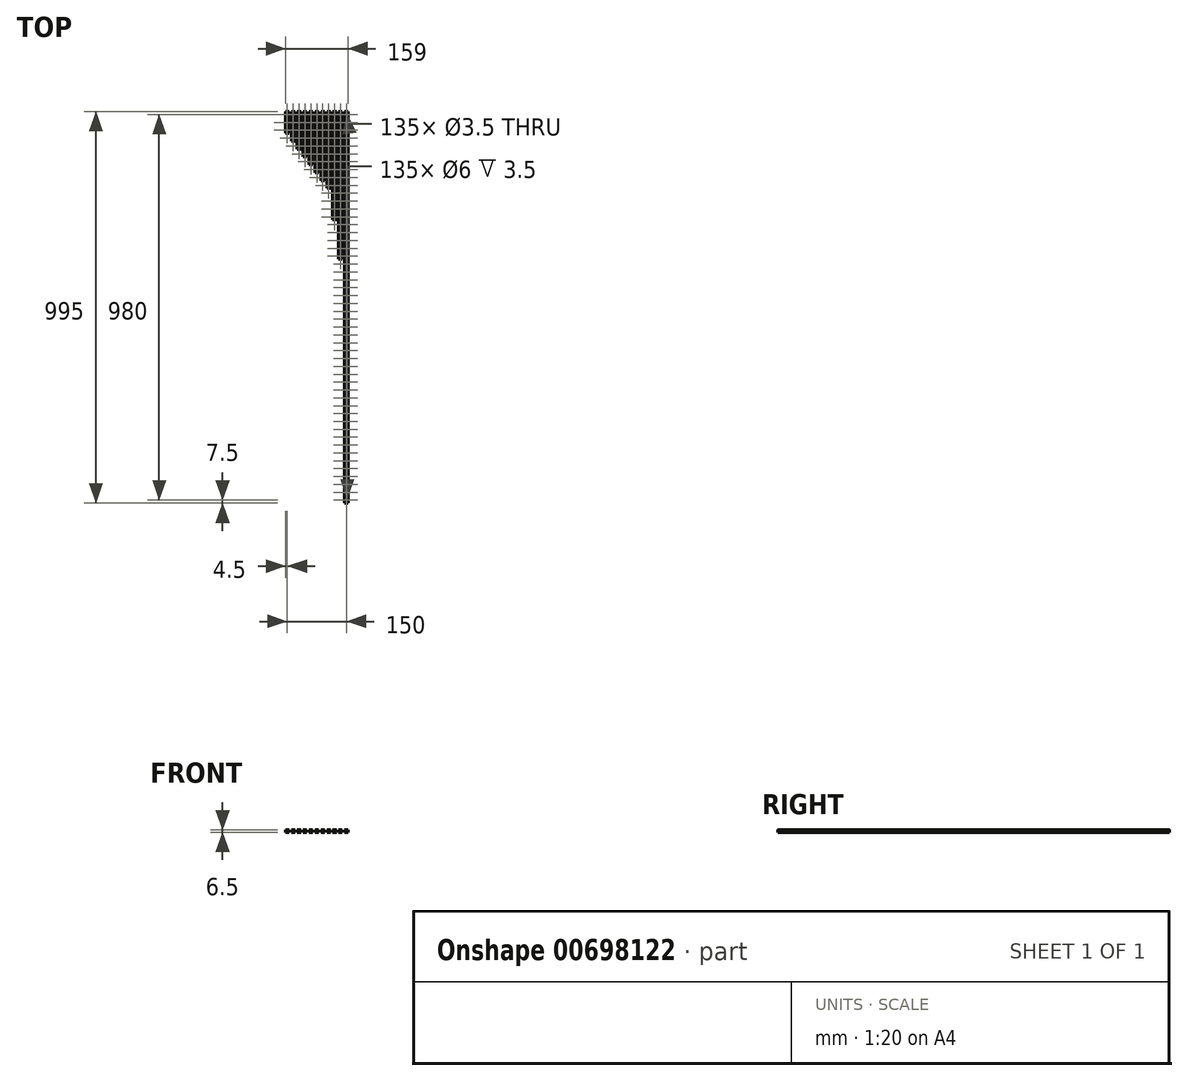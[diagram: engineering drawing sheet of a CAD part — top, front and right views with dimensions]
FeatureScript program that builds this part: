
annotation { "Feature Type Name" : "Feature", "Feature Type Description" : "" }
export const myFeature = defineFeature(function(context is Context, id is Id, definition is map)
    precondition{}
    {
        {
            var Q0;
            Q0=qCreatedBy(makeId("Front.planeOp"),FACE);
            var sketch = newSketch(context, id + "F0", { "sketchPlane" : qUnion([Q0])});
            skPoint(sketch, "E0.middle", {"position": v(0, 0) * mm});
            skLineSegment(sketch, "E1.bottom", {"start": v(4.15, -3.25) * mm, "end": v(-4.15, -3.25) * mm});
            skLineSegment(sketch, "E1.top", {"start": v(4.15, 3.25) * mm, "end": v(-4.15, 3.25) * mm});
            skLineSegment(sketch, "E1.left", {"start": v(4.5, -2.9) * mm, "end": v(4.5, 0.28) * mm});
            skLineSegment(sketch, "E1.right", {"start": v(-4.5, -2.9) * mm, "end": v(-4.5, 0.28) * mm});
            skArc(sketch, "E2", {"start": v(-4.5, 0.28) * mm, "mid": v(-4.1, 0.49) * mm, "end": v(-3.83, 0.85) * mm});
            skArc(sketch, "E3", {"start": v(4.5, 2.22) * mm, "mid": v(4.1, 2.01) * mm, "end": v(3.83, 1.65) * mm});
            skLineSegment(sketch, "E4", {"start": v(3.3, 1.65) * mm, "end": v(3.83, 1.65) * mm});
            skLineSegment(sketch, "E5", {"start": v(3.3, 0.85) * mm, "end": v(3.83, 0.85) * mm});
            skLineSegment(sketch, "E6", {"start": v(-3.3, 0.85) * mm, "end": v(-3.83, 0.85) * mm});
            skLineSegment(sketch, "E7", {"start": v(-3.3, 1.65) * mm, "end": v(-3.83, 1.65) * mm});
            skLineSegment(sketch, "E8", {"start": v(-4.5, 2.9) * mm, "end": v(-4.15, 3.25) * mm});
            skLineSegment(sketch, "E9.MirrorCS", {"start": v(4.5, 2.9) * mm, "end": v(4.15, 3.25) * mm});
            skLineSegment(sketch, "E10.MirrorCS", {"start": v(4.5, -2.9) * mm, "end": v(4.15, -3.25) * mm});
            skLineSegment(sketch, "E11.MirrorCS", {"start": v(-4.5, -2.9) * mm, "end": v(-4.15, -3.25) * mm});
            skPoint(sketch, "E12.orphan", {"position": v(-4.5, 3.25) * mm});
            skLineSegment(sketch, "E13.trimOffspring", {"start": v(-4.5, 2.22) * mm, "end": v(-4.5, 2.9) * mm});
            skArc(sketch, "E14.trimOffspring", {"start": v(-3.83, 1.65) * mm, "mid": v(-4.1, 2.01) * mm, "end": v(-4.5, 2.22) * mm});
            skPoint(sketch, "E15.orphan", {"position": v(4.5, 3.25) * mm});
            skLineSegment(sketch, "E16.trimOffspring", {"start": v(4.5, 2.22) * mm, "end": v(4.5, 2.9) * mm});
            skArc(sketch, "E17.trimOffspring", {"start": v(3.83, 0.85) * mm, "mid": v(4.1, 0.49) * mm, "end": v(4.5, 0.28) * mm});
            skPoint(sketch, "E18.orphan", {"position": v(4.5, -3.25) * mm});
            skPoint(sketch, "E19.orphan", {"position": v(-4.5, -3.25) * mm});
            skLineSegment(sketch, "E20", {"start": v(-3.3, 1.65) * mm, "end": v(-3.3, 0.85) * mm});
            skLineSegment(sketch, "E21", {"start": v(3.3, 1.65) * mm, "end": v(3.3, 0.85) * mm});
            skLineSegment(sketch, "E22", {"start": v(-4.75, 1.25) * mm, "end": v(4.75, 1.25) * mm, "construction": true});
            skLineSegment(sketch, "E23.1.0.0", {"start": v(10.25, 1.25) * mm, "end": v(19.75, 1.25) * mm, "construction": true});
            skLineSegment(sketch, "E23.1.0.1", {"start": v(10.5, -2.9) * mm, "end": v(10.5, 0.28) * mm});
            skLineSegment(sketch, "E23.1.0.2", {"start": v(19.5, -2.9) * mm, "end": v(19.5, 0.28) * mm});
            skLineSegment(sketch, "E23.1.0.3", {"start": v(19.15, -3.25) * mm, "end": v(10.85, -3.25) * mm});
            skLineSegment(sketch, "E23.1.0.4", {"start": v(19.15, 3.25) * mm, "end": v(10.85, 3.25) * mm});
            skPoint(sketch, "E23.1.0.5", {"position": v(15, 0) * mm});
            skPoint(sketch, "E23.1.0.6", {"position": v(10.5, -3.25) * mm});
            skPoint(sketch, "E23.1.0.7", {"position": v(10.5, 3.25) * mm});
            skPoint(sketch, "E23.1.0.8", {"position": v(19.5, 3.25) * mm});
            skPoint(sketch, "E23.1.0.9", {"position": v(19.5, -3.25) * mm});
            skPoint(sketch, "E23.1.0.10", {"position": v(15, 0) * mm});
            skLineSegment(sketch, "E23.1.0.11", {"start": v(19.5, -2.9) * mm, "end": v(19.15, -3.25) * mm});
            skLineSegment(sketch, "E23.1.0.12", {"start": v(19.5, 2.9) * mm, "end": v(19.15, 3.25) * mm});
            skLineSegment(sketch, "E23.1.0.13", {"start": v(10.5, -2.9) * mm, "end": v(10.85, -3.25) * mm});
            skLineSegment(sketch, "E23.1.0.14", {"start": v(11.7, 1.65) * mm, "end": v(11.17, 1.65) * mm});
            skLineSegment(sketch, "E23.1.0.15", {"start": v(10.5, 2.22) * mm, "end": v(10.5, 2.9) * mm});
            skLineSegment(sketch, "E23.1.0.16", {"start": v(19.5, 2.22) * mm, "end": v(19.5, 2.9) * mm});
            skArc(sketch, "E23.1.0.17", {"start": v(18.83, 0.85) * mm, "mid": v(19.1, 0.49) * mm, "end": v(19.5, 0.28) * mm});
            skLineSegment(sketch, "E23.1.0.18", {"start": v(11.7, 1.65) * mm, "end": v(11.7, 0.85) * mm});
            skLineSegment(sketch, "E23.1.0.19", {"start": v(18.3, 0.85) * mm, "end": v(18.83, 0.85) * mm});
            skLineSegment(sketch, "E23.1.0.20", {"start": v(11.7, 0.85) * mm, "end": v(11.17, 0.85) * mm});
            skArc(sketch, "E23.1.0.21", {"start": v(10.5, 0.28) * mm, "mid": v(10.9, 0.49) * mm, "end": v(11.17, 0.85) * mm});
            skLineSegment(sketch, "E23.1.0.22", {"start": v(10.5, 2.9) * mm, "end": v(10.85, 3.25) * mm});
            skArc(sketch, "E23.1.0.23", {"start": v(11.17, 1.65) * mm, "mid": v(10.9, 2.01) * mm, "end": v(10.5, 2.22) * mm});
            skLineSegment(sketch, "E23.1.0.24", {"start": v(18.3, 1.65) * mm, "end": v(18.83, 1.65) * mm});
            skArc(sketch, "E23.1.0.25", {"start": v(19.5, 2.22) * mm, "mid": v(19.1, 2.01) * mm, "end": v(18.83, 1.65) * mm});
            skArc(sketch, "E23.1.0.26", {"start": v(18.83, 0.85) * mm, "mid": v(19.1, 0.49) * mm, "end": v(19.5, 0.28) * mm});
            skLineSegment(sketch, "E23.1.0.27", {"start": v(18.3, 1.65) * mm, "end": v(18.3, 0.85) * mm});
            skLineSegment(sketch, "E23.2.0.0", {"start": v(25.25, 1.25) * mm, "end": v(34.75, 1.25) * mm, "construction": true});
            skLineSegment(sketch, "E23.2.0.1", {"start": v(25.5, -2.9) * mm, "end": v(25.5, 0.28) * mm});
            skLineSegment(sketch, "E23.2.0.2", {"start": v(34.5, -2.9) * mm, "end": v(34.5, 0.28) * mm});
            skLineSegment(sketch, "E23.2.0.3", {"start": v(34.15, -3.25) * mm, "end": v(25.85, -3.25) * mm});
            skLineSegment(sketch, "E23.2.0.4", {"start": v(34.15, 3.25) * mm, "end": v(25.85, 3.25) * mm});
            skPoint(sketch, "E23.2.0.5", {"position": v(30, 0) * mm});
            skPoint(sketch, "E23.2.0.6", {"position": v(25.5, -3.25) * mm});
            skPoint(sketch, "E23.2.0.7", {"position": v(25.5, 3.25) * mm});
            skPoint(sketch, "E23.2.0.8", {"position": v(34.5, 3.25) * mm});
            skPoint(sketch, "E23.2.0.9", {"position": v(34.5, -3.25) * mm});
            skPoint(sketch, "E23.2.0.10", {"position": v(30, 0) * mm});
            skLineSegment(sketch, "E23.2.0.11", {"start": v(34.5, -2.9) * mm, "end": v(34.15, -3.25) * mm});
            skLineSegment(sketch, "E23.2.0.12", {"start": v(34.5, 2.9) * mm, "end": v(34.15, 3.25) * mm});
            skLineSegment(sketch, "E23.2.0.13", {"start": v(25.5, -2.9) * mm, "end": v(25.85, -3.25) * mm});
            skLineSegment(sketch, "E23.2.0.14", {"start": v(26.7, 1.65) * mm, "end": v(26.17, 1.65) * mm});
            skLineSegment(sketch, "E23.2.0.15", {"start": v(25.5, 2.22) * mm, "end": v(25.5, 2.9) * mm});
            skLineSegment(sketch, "E23.2.0.16", {"start": v(34.5, 2.22) * mm, "end": v(34.5, 2.9) * mm});
            skArc(sketch, "E23.2.0.17", {"start": v(33.83, 0.85) * mm, "mid": v(34.1, 0.49) * mm, "end": v(34.5, 0.28) * mm});
            skLineSegment(sketch, "E23.2.0.18", {"start": v(26.7, 1.65) * mm, "end": v(26.7, 0.85) * mm});
            skLineSegment(sketch, "E23.2.0.19", {"start": v(33.3, 0.85) * mm, "end": v(33.83, 0.85) * mm});
            skLineSegment(sketch, "E23.2.0.20", {"start": v(26.7, 0.85) * mm, "end": v(26.17, 0.85) * mm});
            skArc(sketch, "E23.2.0.21", {"start": v(25.5, 0.28) * mm, "mid": v(25.9, 0.49) * mm, "end": v(26.17, 0.85) * mm});
            skLineSegment(sketch, "E23.2.0.22", {"start": v(25.5, 2.9) * mm, "end": v(25.85, 3.25) * mm});
            skArc(sketch, "E23.2.0.23", {"start": v(26.17, 1.65) * mm, "mid": v(25.9, 2.01) * mm, "end": v(25.5, 2.22) * mm});
            skLineSegment(sketch, "E23.2.0.24", {"start": v(33.3, 1.65) * mm, "end": v(33.83, 1.65) * mm});
            skArc(sketch, "E23.2.0.25", {"start": v(34.5, 2.22) * mm, "mid": v(34.1, 2.01) * mm, "end": v(33.83, 1.65) * mm});
            skArc(sketch, "E23.2.0.26", {"start": v(33.83, 0.85) * mm, "mid": v(34.1, 0.49) * mm, "end": v(34.5, 0.28) * mm});
            skLineSegment(sketch, "E23.2.0.27", {"start": v(33.3, 1.65) * mm, "end": v(33.3, 0.85) * mm});
            skLineSegment(sketch, "E23.3.0.0", {"start": v(40.25, 1.25) * mm, "end": v(49.75, 1.25) * mm, "construction": true});
            skLineSegment(sketch, "E23.3.0.1", {"start": v(40.5, -2.9) * mm, "end": v(40.5, 0.28) * mm});
            skLineSegment(sketch, "E23.3.0.2", {"start": v(49.5, -2.9) * mm, "end": v(49.5, 0.28) * mm});
            skLineSegment(sketch, "E23.3.0.3", {"start": v(49.15, -3.25) * mm, "end": v(40.85, -3.25) * mm});
            skLineSegment(sketch, "E23.3.0.4", {"start": v(49.15, 3.25) * mm, "end": v(40.85, 3.25) * mm});
            skPoint(sketch, "E23.3.0.5", {"position": v(45, 0) * mm});
            skPoint(sketch, "E23.3.0.6", {"position": v(40.5, -3.25) * mm});
            skPoint(sketch, "E23.3.0.7", {"position": v(40.5, 3.25) * mm});
            skPoint(sketch, "E23.3.0.8", {"position": v(49.5, 3.25) * mm});
            skPoint(sketch, "E23.3.0.9", {"position": v(49.5, -3.25) * mm});
            skPoint(sketch, "E23.3.0.10", {"position": v(45, 0) * mm});
            skLineSegment(sketch, "E23.3.0.11", {"start": v(49.5, -2.9) * mm, "end": v(49.15, -3.25) * mm});
            skLineSegment(sketch, "E23.3.0.12", {"start": v(49.5, 2.9) * mm, "end": v(49.15, 3.25) * mm});
            skLineSegment(sketch, "E23.3.0.13", {"start": v(40.5, -2.9) * mm, "end": v(40.85, -3.25) * mm});
            skLineSegment(sketch, "E23.3.0.14", {"start": v(41.7, 1.65) * mm, "end": v(41.17, 1.65) * mm});
            skLineSegment(sketch, "E23.3.0.15", {"start": v(40.5, 2.22) * mm, "end": v(40.5, 2.9) * mm});
            skLineSegment(sketch, "E23.3.0.16", {"start": v(49.5, 2.22) * mm, "end": v(49.5, 2.9) * mm});
            skArc(sketch, "E23.3.0.17", {"start": v(48.83, 0.85) * mm, "mid": v(49.1, 0.49) * mm, "end": v(49.5, 0.28) * mm});
            skLineSegment(sketch, "E23.3.0.18", {"start": v(41.7, 1.65) * mm, "end": v(41.7, 0.85) * mm});
            skLineSegment(sketch, "E23.3.0.19", {"start": v(48.3, 0.85) * mm, "end": v(48.83, 0.85) * mm});
            skLineSegment(sketch, "E23.3.0.20", {"start": v(41.7, 0.85) * mm, "end": v(41.17, 0.85) * mm});
            skArc(sketch, "E23.3.0.21", {"start": v(40.5, 0.28) * mm, "mid": v(40.9, 0.49) * mm, "end": v(41.17, 0.85) * mm});
            skLineSegment(sketch, "E23.3.0.22", {"start": v(40.5, 2.9) * mm, "end": v(40.85, 3.25) * mm});
            skArc(sketch, "E23.3.0.23", {"start": v(41.17, 1.65) * mm, "mid": v(40.9, 2.01) * mm, "end": v(40.5, 2.22) * mm});
            skLineSegment(sketch, "E23.3.0.24", {"start": v(48.3, 1.65) * mm, "end": v(48.83, 1.65) * mm});
            skArc(sketch, "E23.3.0.25", {"start": v(49.5, 2.22) * mm, "mid": v(49.1, 2.01) * mm, "end": v(48.83, 1.65) * mm});
            skArc(sketch, "E23.3.0.26", {"start": v(48.83, 0.85) * mm, "mid": v(49.1, 0.49) * mm, "end": v(49.5, 0.28) * mm});
            skLineSegment(sketch, "E23.3.0.27", {"start": v(48.3, 1.65) * mm, "end": v(48.3, 0.85) * mm});
            skLineSegment(sketch, "E23.4.0.0", {"start": v(55.25, 1.25) * mm, "end": v(64.75, 1.25) * mm, "construction": true});
            skLineSegment(sketch, "E23.4.0.1", {"start": v(55.5, -2.9) * mm, "end": v(55.5, 0.28) * mm});
            skLineSegment(sketch, "E23.4.0.2", {"start": v(64.5, -2.9) * mm, "end": v(64.5, 0.28) * mm});
            skLineSegment(sketch, "E23.4.0.3", {"start": v(64.15, -3.25) * mm, "end": v(55.85, -3.25) * mm});
            skLineSegment(sketch, "E23.4.0.4", {"start": v(64.15, 3.25) * mm, "end": v(55.85, 3.25) * mm});
            skPoint(sketch, "E23.4.0.5", {"position": v(60, 0) * mm});
            skPoint(sketch, "E23.4.0.6", {"position": v(55.5, -3.25) * mm});
            skPoint(sketch, "E23.4.0.7", {"position": v(55.5, 3.25) * mm});
            skPoint(sketch, "E23.4.0.8", {"position": v(64.5, 3.25) * mm});
            skPoint(sketch, "E23.4.0.9", {"position": v(64.5, -3.25) * mm});
            skPoint(sketch, "E23.4.0.10", {"position": v(60, 0) * mm});
            skLineSegment(sketch, "E23.4.0.11", {"start": v(64.5, -2.9) * mm, "end": v(64.15, -3.25) * mm});
            skLineSegment(sketch, "E23.4.0.12", {"start": v(64.5, 2.9) * mm, "end": v(64.15, 3.25) * mm});
            skLineSegment(sketch, "E23.4.0.13", {"start": v(55.5, -2.9) * mm, "end": v(55.85, -3.25) * mm});
            skLineSegment(sketch, "E23.4.0.14", {"start": v(56.7, 1.65) * mm, "end": v(56.17, 1.65) * mm});
            skLineSegment(sketch, "E23.4.0.15", {"start": v(55.5, 2.22) * mm, "end": v(55.5, 2.9) * mm});
            skLineSegment(sketch, "E23.4.0.16", {"start": v(64.5, 2.22) * mm, "end": v(64.5, 2.9) * mm});
            skArc(sketch, "E23.4.0.17", {"start": v(63.83, 0.85) * mm, "mid": v(64.1, 0.49) * mm, "end": v(64.5, 0.28) * mm});
            skLineSegment(sketch, "E23.4.0.18", {"start": v(56.7, 1.65) * mm, "end": v(56.7, 0.85) * mm});
            skLineSegment(sketch, "E23.4.0.19", {"start": v(63.3, 0.85) * mm, "end": v(63.83, 0.85) * mm});
            skLineSegment(sketch, "E23.4.0.20", {"start": v(56.7, 0.85) * mm, "end": v(56.17, 0.85) * mm});
            skArc(sketch, "E23.4.0.21", {"start": v(55.5, 0.28) * mm, "mid": v(55.9, 0.49) * mm, "end": v(56.17, 0.85) * mm});
            skLineSegment(sketch, "E23.4.0.22", {"start": v(55.5, 2.9) * mm, "end": v(55.85, 3.25) * mm});
            skArc(sketch, "E23.4.0.23", {"start": v(56.17, 1.65) * mm, "mid": v(55.9, 2.01) * mm, "end": v(55.5, 2.22) * mm});
            skLineSegment(sketch, "E23.4.0.24", {"start": v(63.3, 1.65) * mm, "end": v(63.83, 1.65) * mm});
            skArc(sketch, "E23.4.0.25", {"start": v(64.5, 2.22) * mm, "mid": v(64.1, 2.01) * mm, "end": v(63.83, 1.65) * mm});
            skArc(sketch, "E23.4.0.26", {"start": v(63.83, 0.85) * mm, "mid": v(64.1, 0.49) * mm, "end": v(64.5, 0.28) * mm});
            skLineSegment(sketch, "E23.4.0.27", {"start": v(63.3, 1.65) * mm, "end": v(63.3, 0.85) * mm});
            skLineSegment(sketch, "E23.5.0.0", {"start": v(70.25, 1.25) * mm, "end": v(79.75, 1.25) * mm, "construction": true});
            skLineSegment(sketch, "E23.5.0.1", {"start": v(70.5, -2.9) * mm, "end": v(70.5, 0.28) * mm});
            skLineSegment(sketch, "E23.5.0.2", {"start": v(79.5, -2.9) * mm, "end": v(79.5, 0.28) * mm});
            skLineSegment(sketch, "E23.5.0.3", {"start": v(79.15, -3.25) * mm, "end": v(70.85, -3.25) * mm});
            skLineSegment(sketch, "E23.5.0.4", {"start": v(79.15, 3.25) * mm, "end": v(70.85, 3.25) * mm});
            skPoint(sketch, "E23.5.0.5", {"position": v(75, 0) * mm});
            skPoint(sketch, "E23.5.0.6", {"position": v(70.5, -3.25) * mm});
            skPoint(sketch, "E23.5.0.7", {"position": v(70.5, 3.25) * mm});
            skPoint(sketch, "E23.5.0.8", {"position": v(79.5, 3.25) * mm});
            skPoint(sketch, "E23.5.0.9", {"position": v(79.5, -3.25) * mm});
            skPoint(sketch, "E23.5.0.10", {"position": v(75, 0) * mm});
            skLineSegment(sketch, "E23.5.0.11", {"start": v(79.5, -2.9) * mm, "end": v(79.15, -3.25) * mm});
            skLineSegment(sketch, "E23.5.0.12", {"start": v(79.5, 2.9) * mm, "end": v(79.15, 3.25) * mm});
            skLineSegment(sketch, "E23.5.0.13", {"start": v(70.5, -2.9) * mm, "end": v(70.85, -3.25) * mm});
            skLineSegment(sketch, "E23.5.0.14", {"start": v(71.7, 1.65) * mm, "end": v(71.17, 1.65) * mm});
            skLineSegment(sketch, "E23.5.0.15", {"start": v(70.5, 2.22) * mm, "end": v(70.5, 2.9) * mm});
            skLineSegment(sketch, "E23.5.0.16", {"start": v(79.5, 2.22) * mm, "end": v(79.5, 2.9) * mm});
            skArc(sketch, "E23.5.0.17", {"start": v(78.83, 0.85) * mm, "mid": v(79.1, 0.49) * mm, "end": v(79.5, 0.28) * mm});
            skLineSegment(sketch, "E23.5.0.18", {"start": v(71.7, 1.65) * mm, "end": v(71.7, 0.85) * mm});
            skLineSegment(sketch, "E23.5.0.19", {"start": v(78.3, 0.85) * mm, "end": v(78.83, 0.85) * mm});
            skLineSegment(sketch, "E23.5.0.20", {"start": v(71.7, 0.85) * mm, "end": v(71.17, 0.85) * mm});
            skArc(sketch, "E23.5.0.21", {"start": v(70.5, 0.28) * mm, "mid": v(70.9, 0.49) * mm, "end": v(71.17, 0.85) * mm});
            skLineSegment(sketch, "E23.5.0.22", {"start": v(70.5, 2.9) * mm, "end": v(70.85, 3.25) * mm});
            skArc(sketch, "E23.5.0.23", {"start": v(71.17, 1.65) * mm, "mid": v(70.9, 2.01) * mm, "end": v(70.5, 2.22) * mm});
            skLineSegment(sketch, "E23.5.0.24", {"start": v(78.3, 1.65) * mm, "end": v(78.83, 1.65) * mm});
            skArc(sketch, "E23.5.0.25", {"start": v(79.5, 2.22) * mm, "mid": v(79.1, 2.01) * mm, "end": v(78.83, 1.65) * mm});
            skArc(sketch, "E23.5.0.26", {"start": v(78.83, 0.85) * mm, "mid": v(79.1, 0.49) * mm, "end": v(79.5, 0.28) * mm});
            skLineSegment(sketch, "E23.5.0.27", {"start": v(78.3, 1.65) * mm, "end": v(78.3, 0.85) * mm});
            skLineSegment(sketch, "E23.6.0.0", {"start": v(85.25, 1.25) * mm, "end": v(94.75, 1.25) * mm, "construction": true});
            skLineSegment(sketch, "E23.6.0.1", {"start": v(85.5, -2.9) * mm, "end": v(85.5, 0.28) * mm});
            skLineSegment(sketch, "E23.6.0.2", {"start": v(94.5, -2.9) * mm, "end": v(94.5, 0.28) * mm});
            skLineSegment(sketch, "E23.6.0.3", {"start": v(94.15, -3.25) * mm, "end": v(85.85, -3.25) * mm});
            skLineSegment(sketch, "E23.6.0.4", {"start": v(94.15, 3.25) * mm, "end": v(85.85, 3.25) * mm});
            skPoint(sketch, "E23.6.0.5", {"position": v(90, 0) * mm});
            skPoint(sketch, "E23.6.0.6", {"position": v(85.5, -3.25) * mm});
            skPoint(sketch, "E23.6.0.7", {"position": v(85.5, 3.25) * mm});
            skPoint(sketch, "E23.6.0.8", {"position": v(94.5, 3.25) * mm});
            skPoint(sketch, "E23.6.0.9", {"position": v(94.5, -3.25) * mm});
            skPoint(sketch, "E23.6.0.10", {"position": v(90, 0) * mm});
            skLineSegment(sketch, "E23.6.0.11", {"start": v(94.5, -2.9) * mm, "end": v(94.15, -3.25) * mm});
            skLineSegment(sketch, "E23.6.0.12", {"start": v(94.5, 2.9) * mm, "end": v(94.15, 3.25) * mm});
            skLineSegment(sketch, "E23.6.0.13", {"start": v(85.5, -2.9) * mm, "end": v(85.85, -3.25) * mm});
            skLineSegment(sketch, "E23.6.0.14", {"start": v(86.7, 1.65) * mm, "end": v(86.17, 1.65) * mm});
            skLineSegment(sketch, "E23.6.0.15", {"start": v(85.5, 2.22) * mm, "end": v(85.5, 2.9) * mm});
            skLineSegment(sketch, "E23.6.0.16", {"start": v(94.5, 2.22) * mm, "end": v(94.5, 2.9) * mm});
            skArc(sketch, "E23.6.0.17", {"start": v(93.83, 0.85) * mm, "mid": v(94.1, 0.49) * mm, "end": v(94.5, 0.28) * mm});
            skLineSegment(sketch, "E23.6.0.18", {"start": v(86.7, 1.65) * mm, "end": v(86.7, 0.85) * mm});
            skLineSegment(sketch, "E23.6.0.19", {"start": v(93.3, 0.85) * mm, "end": v(93.83, 0.85) * mm});
            skLineSegment(sketch, "E23.6.0.20", {"start": v(86.7, 0.85) * mm, "end": v(86.17, 0.85) * mm});
            skArc(sketch, "E23.6.0.21", {"start": v(85.5, 0.28) * mm, "mid": v(85.9, 0.49) * mm, "end": v(86.17, 0.85) * mm});
            skLineSegment(sketch, "E23.6.0.22", {"start": v(85.5, 2.9) * mm, "end": v(85.85, 3.25) * mm});
            skArc(sketch, "E23.6.0.23", {"start": v(86.17, 1.65) * mm, "mid": v(85.9, 2.01) * mm, "end": v(85.5, 2.22) * mm});
            skLineSegment(sketch, "E23.6.0.24", {"start": v(93.3, 1.65) * mm, "end": v(93.83, 1.65) * mm});
            skArc(sketch, "E23.6.0.25", {"start": v(94.5, 2.22) * mm, "mid": v(94.1, 2.01) * mm, "end": v(93.83, 1.65) * mm});
            skArc(sketch, "E23.6.0.26", {"start": v(93.83, 0.85) * mm, "mid": v(94.1, 0.49) * mm, "end": v(94.5, 0.28) * mm});
            skLineSegment(sketch, "E23.6.0.27", {"start": v(93.3, 1.65) * mm, "end": v(93.3, 0.85) * mm});
            skLineSegment(sketch, "E23.direction1", {"start": v(-4.5, -3.25) * mm, "end": v(10.5, -3.25) * mm, "construction": true});
            skLineSegment(sketch, "E24.0.7.0", {"start": v(100.25, 1.25) * mm, "end": v(109.75, 1.25) * mm, "construction": true});
            skLineSegment(sketch, "E24.3.7.0", {"start": v(100.5, -2.9) * mm, "end": v(100.5, 0.28) * mm});
            skLineSegment(sketch, "E24.6.7.0", {"start": v(109.5, -2.9) * mm, "end": v(109.5, 0.28) * mm});
            skLineSegment(sketch, "E24.9.7.0", {"start": v(109.15, -3.25) * mm, "end": v(100.85, -3.25) * mm});
            skLineSegment(sketch, "E24.12.7.0", {"start": v(109.15, 3.25) * mm, "end": v(100.85, 3.25) * mm});
            skPoint(sketch, "E24.15.7.0", {"position": v(105, 0) * mm});
            skPoint(sketch, "E24.16.7.0", {"position": v(100.5, -3.25) * mm});
            skPoint(sketch, "E24.17.7.0", {"position": v(100.5, 3.25) * mm});
            skPoint(sketch, "E24.18.7.0", {"position": v(109.5, 3.25) * mm});
            skPoint(sketch, "E24.19.7.0", {"position": v(109.5, -3.25) * mm});
            skPoint(sketch, "E24.20.7.0", {"position": v(105, 0) * mm});
            skLineSegment(sketch, "E24.21.7.0", {"start": v(109.5, -2.9) * mm, "end": v(109.15, -3.25) * mm});
            skLineSegment(sketch, "E24.24.7.0", {"start": v(109.5, 2.9) * mm, "end": v(109.15, 3.25) * mm});
            skLineSegment(sketch, "E24.27.7.0", {"start": v(100.5, -2.9) * mm, "end": v(100.85, -3.25) * mm});
            skLineSegment(sketch, "E24.30.7.0", {"start": v(101.7, 1.65) * mm, "end": v(101.17, 1.65) * mm});
            skLineSegment(sketch, "E24.33.7.0", {"start": v(100.5, 2.22) * mm, "end": v(100.5, 2.9) * mm});
            skLineSegment(sketch, "E24.36.7.0", {"start": v(109.5, 2.22) * mm, "end": v(109.5, 2.9) * mm});
            skArc(sketch, "E24.39.7.0", {"start": v(108.83, 0.85) * mm, "mid": v(109.1, 0.49) * mm, "end": v(109.5, 0.28) * mm});
            skLineSegment(sketch, "E24.43.7.0", {"start": v(101.7, 1.65) * mm, "end": v(101.7, 0.85) * mm});
            skLineSegment(sketch, "E24.46.7.0", {"start": v(108.3, 0.85) * mm, "end": v(108.83, 0.85) * mm});
            skLineSegment(sketch, "E24.49.7.0", {"start": v(101.7, 0.85) * mm, "end": v(101.17, 0.85) * mm});
            skArc(sketch, "E24.52.7.0", {"start": v(100.5, 0.28) * mm, "mid": v(100.9, 0.49) * mm, "end": v(101.17, 0.85) * mm});
            skLineSegment(sketch, "E24.56.7.0", {"start": v(100.5, 2.9) * mm, "end": v(100.85, 3.25) * mm});
            skArc(sketch, "E24.59.7.0", {"start": v(101.17, 1.65) * mm, "mid": v(100.9, 2.01) * mm, "end": v(100.5, 2.22) * mm});
            skLineSegment(sketch, "E24.63.7.0", {"start": v(108.3, 1.65) * mm, "end": v(108.83, 1.65) * mm});
            skArc(sketch, "E24.66.7.0", {"start": v(109.5, 2.22) * mm, "mid": v(109.1, 2.01) * mm, "end": v(108.83, 1.65) * mm});
            skArc(sketch, "E24.70.7.0", {"start": v(108.83, 0.85) * mm, "mid": v(109.1, 0.49) * mm, "end": v(109.5, 0.28) * mm});
            skLineSegment(sketch, "E24.74.7.0", {"start": v(108.3, 1.65) * mm, "end": v(108.3, 0.85) * mm});
            skLineSegment(sketch, "E24.0.8.0", {"start": v(115.25, 1.25) * mm, "end": v(124.75, 1.25) * mm, "construction": true});
            skLineSegment(sketch, "E24.3.8.0", {"start": v(115.5, -2.9) * mm, "end": v(115.5, 0.28) * mm});
            skLineSegment(sketch, "E24.6.8.0", {"start": v(124.5, -2.9) * mm, "end": v(124.5, 0.28) * mm});
            skLineSegment(sketch, "E24.9.8.0", {"start": v(124.15, -3.25) * mm, "end": v(115.85, -3.25) * mm});
            skLineSegment(sketch, "E24.12.8.0", {"start": v(124.15, 3.25) * mm, "end": v(115.85, 3.25) * mm});
            skPoint(sketch, "E24.15.8.0", {"position": v(120, 0) * mm});
            skPoint(sketch, "E24.16.8.0", {"position": v(115.5, -3.25) * mm});
            skPoint(sketch, "E24.17.8.0", {"position": v(115.5, 3.25) * mm});
            skPoint(sketch, "E24.18.8.0", {"position": v(124.5, 3.25) * mm});
            skPoint(sketch, "E24.19.8.0", {"position": v(124.5, -3.25) * mm});
            skPoint(sketch, "E24.20.8.0", {"position": v(120, 0) * mm});
            skLineSegment(sketch, "E24.21.8.0", {"start": v(124.5, -2.9) * mm, "end": v(124.15, -3.25) * mm});
            skLineSegment(sketch, "E24.24.8.0", {"start": v(124.5, 2.9) * mm, "end": v(124.15, 3.25) * mm});
            skLineSegment(sketch, "E24.27.8.0", {"start": v(115.5, -2.9) * mm, "end": v(115.85, -3.25) * mm});
            skLineSegment(sketch, "E24.30.8.0", {"start": v(116.7, 1.65) * mm, "end": v(116.17, 1.65) * mm});
            skLineSegment(sketch, "E24.33.8.0", {"start": v(115.5, 2.22) * mm, "end": v(115.5, 2.9) * mm});
            skLineSegment(sketch, "E24.36.8.0", {"start": v(124.5, 2.22) * mm, "end": v(124.5, 2.9) * mm});
            skArc(sketch, "E24.39.8.0", {"start": v(123.83, 0.85) * mm, "mid": v(124.1, 0.49) * mm, "end": v(124.5, 0.28) * mm});
            skLineSegment(sketch, "E24.43.8.0", {"start": v(116.7, 1.65) * mm, "end": v(116.7, 0.85) * mm});
            skLineSegment(sketch, "E24.46.8.0", {"start": v(123.3, 0.85) * mm, "end": v(123.83, 0.85) * mm});
            skLineSegment(sketch, "E24.49.8.0", {"start": v(116.7, 0.85) * mm, "end": v(116.17, 0.85) * mm});
            skArc(sketch, "E24.52.8.0", {"start": v(115.5, 0.28) * mm, "mid": v(115.9, 0.49) * mm, "end": v(116.17, 0.85) * mm});
            skLineSegment(sketch, "E24.56.8.0", {"start": v(115.5, 2.9) * mm, "end": v(115.85, 3.25) * mm});
            skArc(sketch, "E24.59.8.0", {"start": v(116.17, 1.65) * mm, "mid": v(115.9, 2.01) * mm, "end": v(115.5, 2.22) * mm});
            skLineSegment(sketch, "E24.63.8.0", {"start": v(123.3, 1.65) * mm, "end": v(123.83, 1.65) * mm});
            skArc(sketch, "E24.66.8.0", {"start": v(124.5, 2.22) * mm, "mid": v(124.1, 2.01) * mm, "end": v(123.83, 1.65) * mm});
            skArc(sketch, "E24.70.8.0", {"start": v(123.83, 0.85) * mm, "mid": v(124.1, 0.49) * mm, "end": v(124.5, 0.28) * mm});
            skLineSegment(sketch, "E24.74.8.0", {"start": v(123.3, 1.65) * mm, "end": v(123.3, 0.85) * mm});
            skLineSegment(sketch, "E24.0.9.0", {"start": v(130.25, 1.25) * mm, "end": v(139.75, 1.25) * mm, "construction": true});
            skLineSegment(sketch, "E24.3.9.0", {"start": v(130.5, -2.9) * mm, "end": v(130.5, 0.28) * mm});
            skLineSegment(sketch, "E24.6.9.0", {"start": v(139.5, -2.9) * mm, "end": v(139.5, 0.28) * mm});
            skLineSegment(sketch, "E24.9.9.0", {"start": v(139.15, -3.25) * mm, "end": v(130.85, -3.25) * mm});
            skLineSegment(sketch, "E24.12.9.0", {"start": v(139.15, 3.25) * mm, "end": v(130.85, 3.25) * mm});
            skPoint(sketch, "E24.15.9.0", {"position": v(135, 0) * mm});
            skPoint(sketch, "E24.16.9.0", {"position": v(130.5, -3.25) * mm});
            skPoint(sketch, "E24.17.9.0", {"position": v(130.5, 3.25) * mm});
            skPoint(sketch, "E24.18.9.0", {"position": v(139.5, 3.25) * mm});
            skPoint(sketch, "E24.19.9.0", {"position": v(139.5, -3.25) * mm});
            skPoint(sketch, "E24.20.9.0", {"position": v(135, 0) * mm});
            skLineSegment(sketch, "E24.21.9.0", {"start": v(139.5, -2.9) * mm, "end": v(139.15, -3.25) * mm});
            skLineSegment(sketch, "E24.24.9.0", {"start": v(139.5, 2.9) * mm, "end": v(139.15, 3.25) * mm});
            skLineSegment(sketch, "E24.27.9.0", {"start": v(130.5, -2.9) * mm, "end": v(130.85, -3.25) * mm});
            skLineSegment(sketch, "E24.30.9.0", {"start": v(131.7, 1.65) * mm, "end": v(131.17, 1.65) * mm});
            skLineSegment(sketch, "E24.33.9.0", {"start": v(130.5, 2.22) * mm, "end": v(130.5, 2.9) * mm});
            skLineSegment(sketch, "E24.36.9.0", {"start": v(139.5, 2.22) * mm, "end": v(139.5, 2.9) * mm});
            skArc(sketch, "E24.39.9.0", {"start": v(138.83, 0.85) * mm, "mid": v(139.1, 0.49) * mm, "end": v(139.5, 0.28) * mm});
            skLineSegment(sketch, "E24.43.9.0", {"start": v(131.7, 1.65) * mm, "end": v(131.7, 0.85) * mm});
            skLineSegment(sketch, "E24.46.9.0", {"start": v(138.3, 0.85) * mm, "end": v(138.83, 0.85) * mm});
            skLineSegment(sketch, "E24.49.9.0", {"start": v(131.7, 0.85) * mm, "end": v(131.17, 0.85) * mm});
            skArc(sketch, "E24.52.9.0", {"start": v(130.5, 0.28) * mm, "mid": v(130.9, 0.49) * mm, "end": v(131.17, 0.85) * mm});
            skLineSegment(sketch, "E24.56.9.0", {"start": v(130.5, 2.9) * mm, "end": v(130.85, 3.25) * mm});
            skArc(sketch, "E24.59.9.0", {"start": v(131.17, 1.65) * mm, "mid": v(130.9, 2.01) * mm, "end": v(130.5, 2.22) * mm});
            skLineSegment(sketch, "E24.63.9.0", {"start": v(138.3, 1.65) * mm, "end": v(138.83, 1.65) * mm});
            skArc(sketch, "E24.66.9.0", {"start": v(139.5, 2.22) * mm, "mid": v(139.1, 2.01) * mm, "end": v(138.83, 1.65) * mm});
            skArc(sketch, "E24.70.9.0", {"start": v(138.83, 0.85) * mm, "mid": v(139.1, 0.49) * mm, "end": v(139.5, 0.28) * mm});
            skLineSegment(sketch, "E24.74.9.0", {"start": v(138.3, 1.65) * mm, "end": v(138.3, 0.85) * mm});
            skLineSegment(sketch, "E24.0.10.0", {"start": v(145.25, 1.25) * mm, "end": v(154.75, 1.25) * mm, "construction": true});
            skLineSegment(sketch, "E24.3.10.0", {"start": v(145.5, -2.9) * mm, "end": v(145.5, 0.28) * mm});
            skLineSegment(sketch, "E24.6.10.0", {"start": v(154.5, -2.9) * mm, "end": v(154.5, 0.28) * mm});
            skLineSegment(sketch, "E24.9.10.0", {"start": v(154.15, -3.25) * mm, "end": v(145.85, -3.25) * mm});
            skLineSegment(sketch, "E24.12.10.0", {"start": v(154.15, 3.25) * mm, "end": v(145.85, 3.25) * mm});
            skPoint(sketch, "E24.15.10.0", {"position": v(150, 0) * mm});
            skPoint(sketch, "E24.16.10.0", {"position": v(145.5, -3.25) * mm});
            skPoint(sketch, "E24.17.10.0", {"position": v(145.5, 3.25) * mm});
            skPoint(sketch, "E24.18.10.0", {"position": v(154.5, 3.25) * mm});
            skPoint(sketch, "E24.19.10.0", {"position": v(154.5, -3.25) * mm});
            skPoint(sketch, "E24.20.10.0", {"position": v(150, 0) * mm});
            skLineSegment(sketch, "E24.21.10.0", {"start": v(154.5, -2.9) * mm, "end": v(154.15, -3.25) * mm});
            skLineSegment(sketch, "E24.24.10.0", {"start": v(154.5, 2.9) * mm, "end": v(154.15, 3.25) * mm});
            skLineSegment(sketch, "E24.27.10.0", {"start": v(145.5, -2.9) * mm, "end": v(145.85, -3.25) * mm});
            skLineSegment(sketch, "E24.30.10.0", {"start": v(146.7, 1.65) * mm, "end": v(146.17, 1.65) * mm});
            skLineSegment(sketch, "E24.33.10.0", {"start": v(145.5, 2.22) * mm, "end": v(145.5, 2.9) * mm});
            skLineSegment(sketch, "E24.36.10.0", {"start": v(154.5, 2.22) * mm, "end": v(154.5, 2.9) * mm});
            skArc(sketch, "E24.39.10.0", {"start": v(153.83, 0.85) * mm, "mid": v(154.1, 0.49) * mm, "end": v(154.5, 0.28) * mm});
            skLineSegment(sketch, "E24.43.10.0", {"start": v(146.7, 1.65) * mm, "end": v(146.7, 0.85) * mm});
            skLineSegment(sketch, "E24.46.10.0", {"start": v(153.3, 0.85) * mm, "end": v(153.83, 0.85) * mm});
            skLineSegment(sketch, "E24.49.10.0", {"start": v(146.7, 0.85) * mm, "end": v(146.17, 0.85) * mm});
            skArc(sketch, "E24.52.10.0", {"start": v(145.5, 0.28) * mm, "mid": v(145.9, 0.49) * mm, "end": v(146.17, 0.85) * mm});
            skLineSegment(sketch, "E24.56.10.0", {"start": v(145.5, 2.9) * mm, "end": v(145.85, 3.25) * mm});
            skArc(sketch, "E24.59.10.0", {"start": v(146.17, 1.65) * mm, "mid": v(145.9, 2.01) * mm, "end": v(145.5, 2.22) * mm});
            skLineSegment(sketch, "E24.63.10.0", {"start": v(153.3, 1.65) * mm, "end": v(153.83, 1.65) * mm});
            skArc(sketch, "E24.66.10.0", {"start": v(154.5, 2.22) * mm, "mid": v(154.1, 2.01) * mm, "end": v(153.83, 1.65) * mm});
            skArc(sketch, "E24.70.10.0", {"start": v(153.83, 0.85) * mm, "mid": v(154.1, 0.49) * mm, "end": v(154.5, 0.28) * mm});
            skLineSegment(sketch, "E24.74.10.0", {"start": v(153.3, 1.65) * mm, "end": v(153.3, 0.85) * mm});
            skSolve(sketch);
        }
        {
            var Q0;
            Q0=makeQuery(id+"F0.imprint","IMPRINT",FACE,{"disambiguationData":[TD([[makeQuery(id+"F0.imprint","IMPRINT",EDGE,{"derivedFrom":sQuery(id+"F0.wireOp",EDGE,"E1.bottom")}),-1.0]])]});
            extrude(context, id + "F1", {"entities" : qUnion([Q0]), "depth" : 55 * mm, "offsetDistance" : 25 * mm});
        }
        {
            var Q0;
            Q0=makeQuery(id+"F0.imprint","IMPRINT",FACE,{"disambiguationData":[TD([[makeQuery(id+"F0.imprint","IMPRINT",EDGE,{"derivedFrom":sQuery(id+"F0.wireOp",EDGE,"E23.1.0.1")}),-1.0]])]});
            extrude(context, id + "F2", {"entities" : qUnion([Q0]), "depth" : 75 * mm, "offsetDistance" : 25 * mm});
        }
        {
            var Q0;
            Q0=makeQuery(id+"F0.imprint","IMPRINT",FACE,{"disambiguationData":[TD([[makeQuery(id+"F0.imprint","IMPRINT",EDGE,{"derivedFrom":sQuery(id+"F0.wireOp",EDGE,"E23.2.0.1")}),-1.0]])]});
            extrude(context, id + "F3", {"entities" : qUnion([Q0]), "depth" : 95 * mm, "offsetDistance" : 25 * mm});
        }
        {
            var Q0;
            Q0=makeQuery(id+"F0.imprint","IMPRINT",FACE,{"disambiguationData":[TD([[makeQuery(id+"F0.imprint","IMPRINT",EDGE,{"derivedFrom":sQuery(id+"F0.wireOp",EDGE,"E23.3.0.1")}),-1.0]])]});
            extrude(context, id + "F4", {"entities" : qUnion([Q0]), "depth" : 115 * mm, "offsetDistance" : 25 * mm});
        }
        {
            var Q0;
            Q0=makeQuery(id+"F0.imprint","IMPRINT",FACE,{"disambiguationData":[TD([[makeQuery(id+"F0.imprint","IMPRINT",EDGE,{"derivedFrom":sQuery(id+"F0.wireOp",EDGE,"E23.4.0.1")}),-1.0]])]});
            extrude(context, id + "F5", {"entities" : qUnion([Q0]), "depth" : 135 * mm, "offsetDistance" : 25 * mm});
        }
        {
            var Q0;
            Q0=makeQuery(id+"F0.imprint","IMPRINT",FACE,{"disambiguationData":[TD([[makeQuery(id+"F0.imprint","IMPRINT",EDGE,{"derivedFrom":sQuery(id+"F0.wireOp",EDGE,"E23.5.0.1")}),-1.0]])]});
            extrude(context, id + "F6", {"entities" : qUnion([Q0]), "depth" : 155 * mm, "offsetDistance" : 25 * mm});
        }
        {
            var Q0;
            Q0=makeQuery(id+"F0.imprint","IMPRINT",FACE,{"disambiguationData":[TD([[makeQuery(id+"F0.imprint","IMPRINT",EDGE,{"derivedFrom":sQuery(id+"F0.wireOp",EDGE,"E23.6.0.1")}),-1.0]])]});
            extrude(context, id + "F7", {"entities" : qUnion([Q0]), "depth" : 175 * mm, "offsetDistance" : 25 * mm});
        }
        {
            var Q0;
            Q0=makeQuery(id+"F0.imprint","IMPRINT",FACE,{"disambiguationData":[TD([[makeQuery(id+"F0.imprint","IMPRINT",EDGE,{"derivedFrom":sQuery(id+"F0.wireOp",EDGE,"E24.3.7.0")}),-1.0]])]});
            extrude(context, id + "F8", {"entities" : qUnion([Q0]), "depth" : 195 * mm, "offsetDistance" : 25 * mm});
        }
        {
            var Q0;
            Q0=makeQuery(id+"F0.imprint","IMPRINT",FACE,{"disambiguationData":[TD([[makeQuery(id+"F0.imprint","IMPRINT",EDGE,{"derivedFrom":sQuery(id+"F0.wireOp",EDGE,"E24.3.8.0")}),-1.0]])]});
            extrude(context, id + "F9", {"entities" : qUnion([Q0]), "depth" : 275 * mm, "offsetDistance" : 25 * mm});
        }
        {
            var Q0;
            Q0=makeQuery(id+"F0.imprint","IMPRINT",FACE,{"disambiguationData":[TD([[makeQuery(id+"F0.imprint","IMPRINT",EDGE,{"derivedFrom":sQuery(id+"F0.wireOp",EDGE,"E24.3.9.0")}),-1.0]])]});
            extrude(context, id + "F10", {"entities" : qUnion([Q0]), "depth" : 375 * mm, "offsetDistance" : 25 * mm});
        }
        {
            var Q0;
            Q0=makeQuery(id+"F0.imprint","IMPRINT",FACE,{"disambiguationData":[TD([[makeQuery(id+"F0.imprint","IMPRINT",EDGE,{"derivedFrom":sQuery(id+"F0.wireOp",EDGE,"E24.3.10.0")}),-1.0]])]});
            extrude(context, id + "F11", {"entities" : qUnion([Q0]), "depth" : 995 * mm, "offsetDistance" : 25 * mm});
        }
        {
            var Q0;
            Q0=makeQuery(id+"F1.opExtrude","SWEPT_FACE",FACE,{"disambiguationData":[OSD([sQuery(id+"F0.wireOp",EDGE,"E1.top")])]});
            var sketch = newSketch(context, id + "F12", { "sketchPlane" : qUnion([Q0])});
            skPoint(sketch, "E25", {"position": v(0, -7.5) * mm});
            skPoint(sketch, "E26.1.0.0", {"position": v(15, -7.5) * mm});
            skPoint(sketch, "E26.2.0.0", {"position": v(30, -7.5) * mm});
            skPoint(sketch, "E26.3.0.0", {"position": v(45, -7.5) * mm});
            skPoint(sketch, "E26.4.0.0", {"position": v(60, -7.5) * mm});
            skPoint(sketch, "E26.5.0.0", {"position": v(75, -7.5) * mm});
            skPoint(sketch, "E26.6.0.0", {"position": v(90, -7.5) * mm});
            skLineSegment(sketch, "E26.direction1", {"start": v(0, -7.5) * mm, "end": v(15, -7.5) * mm, "construction": true});
            skPoint(sketch, "E27.1.0.0", {"position": v(0, -27.5) * mm});
            skPoint(sketch, "E27.1.0.1", {"position": v(15, -27.5) * mm});
            skPoint(sketch, "E27.1.0.2", {"position": v(30, -27.5) * mm});
            skPoint(sketch, "E27.1.0.3", {"position": v(45, -27.5) * mm});
            skPoint(sketch, "E27.1.0.4", {"position": v(60, -27.5) * mm});
            skPoint(sketch, "E27.1.0.5", {"position": v(75, -27.5) * mm});
            skPoint(sketch, "E27.1.0.6", {"position": v(90, -27.5) * mm});
            skPoint(sketch, "E27.2.0.0", {"position": v(0, -47.5) * mm});
            skPoint(sketch, "E27.2.0.1", {"position": v(15, -47.5) * mm});
            skPoint(sketch, "E27.2.0.2", {"position": v(30, -47.5) * mm});
            skPoint(sketch, "E27.2.0.3", {"position": v(45, -47.5) * mm});
            skPoint(sketch, "E27.2.0.4", {"position": v(60, -47.5) * mm});
            skPoint(sketch, "E27.2.0.5", {"position": v(75, -47.5) * mm});
            skPoint(sketch, "E27.2.0.6", {"position": v(90, -47.5) * mm});
            skPoint(sketch, "E27.3.0.0", {"position": v(0, -67.5) * mm});
            skPoint(sketch, "E27.3.0.1", {"position": v(15, -67.5) * mm});
            skPoint(sketch, "E27.3.0.2", {"position": v(30, -67.5) * mm});
            skPoint(sketch, "E27.3.0.3", {"position": v(45, -67.5) * mm});
            skPoint(sketch, "E27.3.0.4", {"position": v(60, -67.5) * mm});
            skPoint(sketch, "E27.3.0.5", {"position": v(75, -67.5) * mm});
            skPoint(sketch, "E27.3.0.6", {"position": v(90, -67.5) * mm});
            skPoint(sketch, "E27.4.0.0", {"position": v(0, -87.5) * mm});
            skPoint(sketch, "E27.4.0.1", {"position": v(15, -87.5) * mm});
            skPoint(sketch, "E27.4.0.2", {"position": v(30, -87.5) * mm});
            skPoint(sketch, "E27.4.0.3", {"position": v(45, -87.5) * mm});
            skPoint(sketch, "E27.4.0.4", {"position": v(60, -87.5) * mm});
            skPoint(sketch, "E27.4.0.5", {"position": v(75, -87.5) * mm});
            skPoint(sketch, "E27.4.0.6", {"position": v(90, -87.5) * mm});
            skPoint(sketch, "E27.5.0.0", {"position": v(0, -107.5) * mm});
            skPoint(sketch, "E27.5.0.1", {"position": v(15, -107.5) * mm});
            skPoint(sketch, "E27.5.0.2", {"position": v(30, -107.5) * mm});
            skPoint(sketch, "E27.5.0.3", {"position": v(45, -107.5) * mm});
            skPoint(sketch, "E27.5.0.4", {"position": v(60, -107.5) * mm});
            skPoint(sketch, "E27.5.0.5", {"position": v(75, -107.5) * mm});
            skPoint(sketch, "E27.5.0.6", {"position": v(90, -107.5) * mm});
            skPoint(sketch, "E27.6.0.0", {"position": v(0, -127.5) * mm});
            skPoint(sketch, "E27.6.0.1", {"position": v(15, -127.5) * mm});
            skPoint(sketch, "E27.6.0.2", {"position": v(30, -127.5) * mm});
            skPoint(sketch, "E27.6.0.3", {"position": v(45, -127.5) * mm});
            skPoint(sketch, "E27.6.0.4", {"position": v(60, -127.5) * mm});
            skPoint(sketch, "E27.6.0.5", {"position": v(75, -127.5) * mm});
            skPoint(sketch, "E27.6.0.6", {"position": v(90, -127.5) * mm});
            skPoint(sketch, "E27.7.0.0", {"position": v(0, -147.5) * mm});
            skPoint(sketch, "E27.7.0.1", {"position": v(15, -147.5) * mm});
            skPoint(sketch, "E27.7.0.2", {"position": v(30, -147.5) * mm});
            skPoint(sketch, "E27.7.0.3", {"position": v(45, -147.5) * mm});
            skPoint(sketch, "E27.7.0.4", {"position": v(60, -147.5) * mm});
            skPoint(sketch, "E27.7.0.5", {"position": v(75, -147.5) * mm});
            skPoint(sketch, "E27.7.0.6", {"position": v(90, -147.5) * mm});
            skPoint(sketch, "E27.8.0.0", {"position": v(0, -167.5) * mm});
            skPoint(sketch, "E27.8.0.1", {"position": v(15, -167.5) * mm});
            skPoint(sketch, "E27.8.0.2", {"position": v(30, -167.5) * mm});
            skPoint(sketch, "E27.8.0.3", {"position": v(45, -167.5) * mm});
            skPoint(sketch, "E27.8.0.4", {"position": v(60, -167.5) * mm});
            skPoint(sketch, "E27.8.0.5", {"position": v(75, -167.5) * mm});
            skPoint(sketch, "E27.8.0.6", {"position": v(90, -167.5) * mm});
            skPoint(sketch, "E27.9.0.0", {"position": v(0, -187.5) * mm});
            skPoint(sketch, "E27.9.0.1", {"position": v(15, -187.5) * mm});
            skPoint(sketch, "E27.9.0.2", {"position": v(30, -187.5) * mm});
            skPoint(sketch, "E27.9.0.3", {"position": v(45, -187.5) * mm});
            skPoint(sketch, "E27.9.0.4", {"position": v(60, -187.5) * mm});
            skPoint(sketch, "E27.9.0.5", {"position": v(75, -187.5) * mm});
            skPoint(sketch, "E27.9.0.6", {"position": v(90, -187.5) * mm});
            skLineSegment(sketch, "E27.direction1", {"start": v(0, -7.5) * mm, "end": v(0, -27.5) * mm, "construction": true});
            skPoint(sketch, "E28.0.7.0", {"position": v(105, -7.5) * mm});
            skPoint(sketch, "E28.0.8.0", {"position": v(120, -7.5) * mm});
            skPoint(sketch, "E28.0.9.0", {"position": v(135, -7.5) * mm});
            skPoint(sketch, "E28.0.10.0", {"position": v(150, -7.5) * mm});
            skPoint(sketch, "E29.1.0.0", {"position": v(150, -27.5) * mm});
            skPoint(sketch, "E29.1.0.1", {"position": v(135, -27.5) * mm});
            skPoint(sketch, "E29.1.0.2", {"position": v(120, -27.5) * mm});
            skPoint(sketch, "E29.1.0.3", {"position": v(105, -27.5) * mm});
            skPoint(sketch, "E29.2.0.0", {"position": v(150, -47.5) * mm});
            skPoint(sketch, "E29.2.0.1", {"position": v(135, -47.5) * mm});
            skPoint(sketch, "E29.2.0.2", {"position": v(120, -47.5) * mm});
            skPoint(sketch, "E29.2.0.3", {"position": v(105, -47.5) * mm});
            skLineSegment(sketch, "E29.direction1", {"start": v(105, -7.5) * mm, "end": v(105, -27.5) * mm, "construction": true});
            skPoint(sketch, "E30.0.3.0", {"position": v(150, -67.5) * mm});
            skPoint(sketch, "E30.1.3.0", {"position": v(135, -67.5) * mm});
            skPoint(sketch, "E30.2.3.0", {"position": v(120, -67.5) * mm});
            skPoint(sketch, "E30.3.3.0", {"position": v(105, -67.5) * mm});
            skPoint(sketch, "E30.0.4.0", {"position": v(150, -87.5) * mm});
            skPoint(sketch, "E30.1.4.0", {"position": v(135, -87.5) * mm});
            skPoint(sketch, "E30.2.4.0", {"position": v(120, -87.5) * mm});
            skPoint(sketch, "E30.3.4.0", {"position": v(105, -87.5) * mm});
            skPoint(sketch, "E30.0.5.0", {"position": v(150, -107.5) * mm});
            skPoint(sketch, "E30.1.5.0", {"position": v(135, -107.5) * mm});
            skPoint(sketch, "E30.2.5.0", {"position": v(120, -107.5) * mm});
            skPoint(sketch, "E30.3.5.0", {"position": v(105, -107.5) * mm});
            skPoint(sketch, "E30.0.6.0", {"position": v(150, -127.5) * mm});
            skPoint(sketch, "E30.1.6.0", {"position": v(135, -127.5) * mm});
            skPoint(sketch, "E30.2.6.0", {"position": v(120, -127.5) * mm});
            skPoint(sketch, "E30.3.6.0", {"position": v(105, -127.5) * mm});
            skPoint(sketch, "E30.0.7.0", {"position": v(150, -147.5) * mm});
            skPoint(sketch, "E30.1.7.0", {"position": v(135, -147.5) * mm});
            skPoint(sketch, "E30.2.7.0", {"position": v(120, -147.5) * mm});
            skPoint(sketch, "E30.3.7.0", {"position": v(105, -147.5) * mm});
            skPoint(sketch, "E30.0.8.0", {"position": v(150, -167.5) * mm});
            skPoint(sketch, "E30.1.8.0", {"position": v(135, -167.5) * mm});
            skPoint(sketch, "E30.2.8.0", {"position": v(120, -167.5) * mm});
            skPoint(sketch, "E30.3.8.0", {"position": v(105, -167.5) * mm});
            skPoint(sketch, "E30.0.9.0", {"position": v(150, -187.5) * mm});
            skPoint(sketch, "E30.1.9.0", {"position": v(135, -187.5) * mm});
            skPoint(sketch, "E30.2.9.0", {"position": v(120, -187.5) * mm});
            skPoint(sketch, "E30.3.9.0", {"position": v(105, -187.5) * mm});
            skPoint(sketch, "E30.0.10.0", {"position": v(150, -207.5) * mm});
            skPoint(sketch, "E30.1.10.0", {"position": v(135, -207.5) * mm});
            skPoint(sketch, "E30.2.10.0", {"position": v(120, -207.5) * mm});
            skPoint(sketch, "E30.3.10.0", {"position": v(105, -207.5) * mm});
            skPoint(sketch, "E30.0.11.0", {"position": v(150, -227.5) * mm});
            skPoint(sketch, "E30.1.11.0", {"position": v(135, -227.5) * mm});
            skPoint(sketch, "E30.2.11.0", {"position": v(120, -227.5) * mm});
            skPoint(sketch, "E30.3.11.0", {"position": v(105, -227.5) * mm});
            skPoint(sketch, "E30.0.12.0", {"position": v(150, -247.5) * mm});
            skPoint(sketch, "E30.1.12.0", {"position": v(135, -247.5) * mm});
            skPoint(sketch, "E30.2.12.0", {"position": v(120, -247.5) * mm});
            skPoint(sketch, "E30.3.12.0", {"position": v(105, -247.5) * mm});
            skPoint(sketch, "E30.0.13.0", {"position": v(150, -267.5) * mm});
            skPoint(sketch, "E30.1.13.0", {"position": v(135, -267.5) * mm});
            skPoint(sketch, "E30.2.13.0", {"position": v(120, -267.5) * mm});
            skPoint(sketch, "E30.3.13.0", {"position": v(105, -267.5) * mm});
            skPoint(sketch, "E30.0.14.0", {"position": v(150, -287.5) * mm});
            skPoint(sketch, "E30.1.14.0", {"position": v(135, -287.5) * mm});
            skPoint(sketch, "E30.2.14.0", {"position": v(120, -287.5) * mm});
            skPoint(sketch, "E30.3.14.0", {"position": v(105, -287.5) * mm});
            skPoint(sketch, "E30.0.15.0", {"position": v(150, -307.5) * mm});
            skPoint(sketch, "E30.1.15.0", {"position": v(135, -307.5) * mm});
            skPoint(sketch, "E30.2.15.0", {"position": v(120, -307.5) * mm});
            skPoint(sketch, "E30.3.15.0", {"position": v(105, -307.5) * mm});
            skPoint(sketch, "E30.0.16.0", {"position": v(150, -327.5) * mm});
            skPoint(sketch, "E30.1.16.0", {"position": v(135, -327.5) * mm});
            skPoint(sketch, "E30.2.16.0", {"position": v(120, -327.5) * mm});
            skPoint(sketch, "E30.3.16.0", {"position": v(105, -327.5) * mm});
            skPoint(sketch, "E30.0.17.0", {"position": v(150, -347.5) * mm});
            skPoint(sketch, "E30.1.17.0", {"position": v(135, -347.5) * mm});
            skPoint(sketch, "E30.2.17.0", {"position": v(120, -347.5) * mm});
            skPoint(sketch, "E30.3.17.0", {"position": v(105, -347.5) * mm});
            skPoint(sketch, "E30.0.18.0", {"position": v(150, -367.5) * mm});
            skPoint(sketch, "E30.1.18.0", {"position": v(135, -367.5) * mm});
            skPoint(sketch, "E30.2.18.0", {"position": v(120, -367.5) * mm});
            skPoint(sketch, "E30.3.18.0", {"position": v(105, -367.5) * mm});
            skPoint(sketch, "E30.0.19.0", {"position": v(150, -387.5) * mm});
            skPoint(sketch, "E30.1.19.0", {"position": v(135, -387.5) * mm});
            skPoint(sketch, "E30.2.19.0", {"position": v(120, -387.5) * mm});
            skPoint(sketch, "E30.3.19.0", {"position": v(105, -387.5) * mm});
            skPoint(sketch, "E30.0.20.0", {"position": v(150, -407.5) * mm});
            skPoint(sketch, "E30.1.20.0", {"position": v(135, -407.5) * mm});
            skPoint(sketch, "E30.2.20.0", {"position": v(120, -407.5) * mm});
            skPoint(sketch, "E30.3.20.0", {"position": v(105, -407.5) * mm});
            skPoint(sketch, "E30.0.21.0", {"position": v(150, -427.5) * mm});
            skPoint(sketch, "E30.1.21.0", {"position": v(135, -427.5) * mm});
            skPoint(sketch, "E30.2.21.0", {"position": v(120, -427.5) * mm});
            skPoint(sketch, "E30.3.21.0", {"position": v(105, -427.5) * mm});
            skPoint(sketch, "E30.0.22.0", {"position": v(150, -447.5) * mm});
            skPoint(sketch, "E30.1.22.0", {"position": v(135, -447.5) * mm});
            skPoint(sketch, "E30.2.22.0", {"position": v(120, -447.5) * mm});
            skPoint(sketch, "E30.3.22.0", {"position": v(105, -447.5) * mm});
            skPoint(sketch, "E30.0.23.0", {"position": v(150, -467.5) * mm});
            skPoint(sketch, "E30.1.23.0", {"position": v(135, -467.5) * mm});
            skPoint(sketch, "E30.2.23.0", {"position": v(120, -467.5) * mm});
            skPoint(sketch, "E30.3.23.0", {"position": v(105, -467.5) * mm});
            skPoint(sketch, "E30.0.24.0", {"position": v(150, -487.5) * mm});
            skPoint(sketch, "E30.1.24.0", {"position": v(135, -487.5) * mm});
            skPoint(sketch, "E30.2.24.0", {"position": v(120, -487.5) * mm});
            skPoint(sketch, "E30.3.24.0", {"position": v(105, -487.5) * mm});
            skPoint(sketch, "E30.0.25.0", {"position": v(150, -507.5) * mm});
            skPoint(sketch, "E30.1.25.0", {"position": v(135, -507.5) * mm});
            skPoint(sketch, "E30.2.25.0", {"position": v(120, -507.5) * mm});
            skPoint(sketch, "E30.3.25.0", {"position": v(105, -507.5) * mm});
            skPoint(sketch, "E30.0.26.0", {"position": v(150, -527.5) * mm});
            skPoint(sketch, "E30.1.26.0", {"position": v(135, -527.5) * mm});
            skPoint(sketch, "E30.2.26.0", {"position": v(120, -527.5) * mm});
            skPoint(sketch, "E30.3.26.0", {"position": v(105, -527.5) * mm});
            skPoint(sketch, "E30.0.27.0", {"position": v(150, -547.5) * mm});
            skPoint(sketch, "E30.1.27.0", {"position": v(135, -547.5) * mm});
            skPoint(sketch, "E30.2.27.0", {"position": v(120, -547.5) * mm});
            skPoint(sketch, "E30.3.27.0", {"position": v(105, -547.5) * mm});
            skPoint(sketch, "E30.0.28.0", {"position": v(150, -567.5) * mm});
            skPoint(sketch, "E30.1.28.0", {"position": v(135, -567.5) * mm});
            skPoint(sketch, "E30.2.28.0", {"position": v(120, -567.5) * mm});
            skPoint(sketch, "E30.3.28.0", {"position": v(105, -567.5) * mm});
            skPoint(sketch, "E30.0.29.0", {"position": v(150, -587.5) * mm});
            skPoint(sketch, "E30.1.29.0", {"position": v(135, -587.5) * mm});
            skPoint(sketch, "E30.2.29.0", {"position": v(120, -587.5) * mm});
            skPoint(sketch, "E30.3.29.0", {"position": v(105, -587.5) * mm});
            skPoint(sketch, "E30.0.30.0", {"position": v(150, -607.5) * mm});
            skPoint(sketch, "E30.1.30.0", {"position": v(135, -607.5) * mm});
            skPoint(sketch, "E30.2.30.0", {"position": v(120, -607.5) * mm});
            skPoint(sketch, "E30.3.30.0", {"position": v(105, -607.5) * mm});
            skPoint(sketch, "E30.0.31.0", {"position": v(150, -627.5) * mm});
            skPoint(sketch, "E30.1.31.0", {"position": v(135, -627.5) * mm});
            skPoint(sketch, "E30.2.31.0", {"position": v(120, -627.5) * mm});
            skPoint(sketch, "E30.3.31.0", {"position": v(105, -627.5) * mm});
            skPoint(sketch, "E30.0.32.0", {"position": v(150, -647.5) * mm});
            skPoint(sketch, "E30.1.32.0", {"position": v(135, -647.5) * mm});
            skPoint(sketch, "E30.2.32.0", {"position": v(120, -647.5) * mm});
            skPoint(sketch, "E30.3.32.0", {"position": v(105, -647.5) * mm});
            skPoint(sketch, "E30.0.33.0", {"position": v(150, -667.5) * mm});
            skPoint(sketch, "E30.1.33.0", {"position": v(135, -667.5) * mm});
            skPoint(sketch, "E30.2.33.0", {"position": v(120, -667.5) * mm});
            skPoint(sketch, "E30.3.33.0", {"position": v(105, -667.5) * mm});
            skPoint(sketch, "E30.0.34.0", {"position": v(150, -687.5) * mm});
            skPoint(sketch, "E30.1.34.0", {"position": v(135, -687.5) * mm});
            skPoint(sketch, "E30.2.34.0", {"position": v(120, -687.5) * mm});
            skPoint(sketch, "E30.3.34.0", {"position": v(105, -687.5) * mm});
            skPoint(sketch, "E30.0.35.0", {"position": v(150, -707.5) * mm});
            skPoint(sketch, "E30.1.35.0", {"position": v(135, -707.5) * mm});
            skPoint(sketch, "E30.2.35.0", {"position": v(120, -707.5) * mm});
            skPoint(sketch, "E30.3.35.0", {"position": v(105, -707.5) * mm});
            skPoint(sketch, "E30.0.36.0", {"position": v(150, -727.5) * mm});
            skPoint(sketch, "E30.1.36.0", {"position": v(135, -727.5) * mm});
            skPoint(sketch, "E30.2.36.0", {"position": v(120, -727.5) * mm});
            skPoint(sketch, "E30.3.36.0", {"position": v(105, -727.5) * mm});
            skPoint(sketch, "E30.0.37.0", {"position": v(150, -747.5) * mm});
            skPoint(sketch, "E30.1.37.0", {"position": v(135, -747.5) * mm});
            skPoint(sketch, "E30.2.37.0", {"position": v(120, -747.5) * mm});
            skPoint(sketch, "E30.3.37.0", {"position": v(105, -747.5) * mm});
            skPoint(sketch, "E30.0.38.0", {"position": v(150, -767.5) * mm});
            skPoint(sketch, "E30.1.38.0", {"position": v(135, -767.5) * mm});
            skPoint(sketch, "E30.2.38.0", {"position": v(120, -767.5) * mm});
            skPoint(sketch, "E30.3.38.0", {"position": v(105, -767.5) * mm});
            skPoint(sketch, "E30.0.39.0", {"position": v(150, -787.5) * mm});
            skPoint(sketch, "E30.1.39.0", {"position": v(135, -787.5) * mm});
            skPoint(sketch, "E30.2.39.0", {"position": v(120, -787.5) * mm});
            skPoint(sketch, "E30.3.39.0", {"position": v(105, -787.5) * mm});
            skPoint(sketch, "E31.0.40.0", {"position": v(150, -807.5) * mm});
            skPoint(sketch, "E31.1.40.0", {"position": v(135, -807.5) * mm});
            skPoint(sketch, "E31.2.40.0", {"position": v(120, -807.5) * mm});
            skPoint(sketch, "E31.3.40.0", {"position": v(105, -807.5) * mm});
            skPoint(sketch, "E31.0.41.0", {"position": v(150, -827.5) * mm});
            skPoint(sketch, "E31.1.41.0", {"position": v(135, -827.5) * mm});
            skPoint(sketch, "E31.2.41.0", {"position": v(120, -827.5) * mm});
            skPoint(sketch, "E31.3.41.0", {"position": v(105, -827.5) * mm});
            skPoint(sketch, "E31.0.42.0", {"position": v(150, -847.5) * mm});
            skPoint(sketch, "E31.1.42.0", {"position": v(135, -847.5) * mm});
            skPoint(sketch, "E31.2.42.0", {"position": v(120, -847.5) * mm});
            skPoint(sketch, "E31.3.42.0", {"position": v(105, -847.5) * mm});
            skPoint(sketch, "E31.0.43.0", {"position": v(150, -867.5) * mm});
            skPoint(sketch, "E31.1.43.0", {"position": v(135, -867.5) * mm});
            skPoint(sketch, "E31.2.43.0", {"position": v(120, -867.5) * mm});
            skPoint(sketch, "E31.3.43.0", {"position": v(105, -867.5) * mm});
            skPoint(sketch, "E31.0.44.0", {"position": v(150, -887.5) * mm});
            skPoint(sketch, "E31.1.44.0", {"position": v(135, -887.5) * mm});
            skPoint(sketch, "E31.2.44.0", {"position": v(120, -887.5) * mm});
            skPoint(sketch, "E31.3.44.0", {"position": v(105, -887.5) * mm});
            skPoint(sketch, "E31.0.45.0", {"position": v(150, -907.5) * mm});
            skPoint(sketch, "E31.1.45.0", {"position": v(135, -907.5) * mm});
            skPoint(sketch, "E31.2.45.0", {"position": v(120, -907.5) * mm});
            skPoint(sketch, "E31.3.45.0", {"position": v(105, -907.5) * mm});
            skPoint(sketch, "E31.0.46.0", {"position": v(150, -927.5) * mm});
            skPoint(sketch, "E31.1.46.0", {"position": v(135, -927.5) * mm});
            skPoint(sketch, "E31.2.46.0", {"position": v(120, -927.5) * mm});
            skPoint(sketch, "E31.3.46.0", {"position": v(105, -927.5) * mm});
            skPoint(sketch, "E31.0.47.0", {"position": v(150, -947.5) * mm});
            skPoint(sketch, "E31.1.47.0", {"position": v(135, -947.5) * mm});
            skPoint(sketch, "E31.2.47.0", {"position": v(120, -947.5) * mm});
            skPoint(sketch, "E31.3.47.0", {"position": v(105, -947.5) * mm});
            skPoint(sketch, "E31.0.48.0", {"position": v(150, -967.5) * mm});
            skPoint(sketch, "E31.1.48.0", {"position": v(135, -967.5) * mm});
            skPoint(sketch, "E31.2.48.0", {"position": v(120, -967.5) * mm});
            skPoint(sketch, "E31.3.48.0", {"position": v(105, -967.5) * mm});
            skPoint(sketch, "E31.0.49.0", {"position": v(150, -987.5) * mm});
            skPoint(sketch, "E31.1.49.0", {"position": v(135, -987.5) * mm});
            skPoint(sketch, "E31.2.49.0", {"position": v(120, -987.5) * mm});
            skPoint(sketch, "E31.3.49.0", {"position": v(105, -987.5) * mm});
            skSolve(sketch);
        }
        {
            var Q0;
            Q0=sQuery(id+"F12.wireOp",VERTEX,"E26.5.0.0");
            var Q1;
            Q1=sQuery(id+"F12.wireOp",VERTEX,"E29.2.0.1");
            var Q2;
            Q2=sQuery(id+"F12.wireOp",VERTEX,"E27.2.0.1");
            var Q3;
            Q3=sQuery(id+"F12.wireOp",VERTEX,"E26.4.0.0");
            var Q4;
            Q4=sQuery(id+"F12.wireOp",VERTEX,"E27.1.0.6");
            var Q5;
            Q5=sQuery(id+"F12.wireOp",VERTEX,"E27.2.0.6");
            var Q6;
            Q6=sQuery(id+"F12.wireOp",VERTEX,"E29.1.0.2");
            var Q7;
            Q7=sQuery(id+"F12.wireOp",VERTEX,"E26.2.0.0");
            var Q8;
            Q8=sQuery(id+"F12.wireOp",VERTEX,"E28.0.7.0");
            var Q9;
            Q9=sQuery(id+"F12.wireOp",VERTEX,"E27.2.0.2");
            var Q10;
            Q10=sQuery(id+"F12.wireOp",VERTEX,"E27.2.0.0");
            var Q11;
            Q11=sQuery(id+"F12.wireOp",VERTEX,"E27.2.0.5");
            var Q12;
            Q12=sQuery(id+"F12.wireOp",VERTEX,"E26.3.0.0");
            var Q13;
            Q13=sQuery(id+"F12.wireOp",VERTEX,"E26.6.0.0");
            var Q14;
            Q14=sQuery(id+"F12.wireOp",VERTEX,"E29.2.0.2");
            var Q15;
            Q15=sQuery(id+"F12.wireOp",VERTEX,"E29.1.0.3");
            var Q16;
            Q16=sQuery(id+"F12.wireOp",VERTEX,"E26.1.0.0");
            var Q17;
            Q17=sQuery(id+"F12.wireOp",VERTEX,"E29.2.0.3");
            var Q18;
            Q18=sQuery(id+"F12.wireOp",VERTEX,"E27.1.0.5");
            var Q19;
            Q19=sQuery(id+"F12.wireOp",VERTEX,"E29.1.0.1");
            var Q20;
            Q20=sQuery(id+"F12.wireOp",VERTEX,"E27.2.0.3");
            var Q21;
            Q21=sQuery(id+"F12.wireOp",VERTEX,"E25");
            var Q22;
            Q22=sQuery(id+"F12.wireOp",VERTEX,"E27.2.0.4");
            var Q23;
            Q23=sQuery(id+"F12.wireOp",VERTEX,"E27.1.0.2");
            var Q24;
            Q24=sQuery(id+"F12.wireOp",VERTEX,"E28.0.8.0");
            var Q25;
            Q25=sQuery(id+"F12.wireOp",VERTEX,"E27.1.0.3");
            var Q26;
            Q26=sQuery(id+"F12.wireOp",VERTEX,"E28.0.9.0");
            var Q27;
            Q27=sQuery(id+"F12.wireOp",VERTEX,"E27.1.0.4");
            var Q28;
            Q28=sQuery(id+"F12.wireOp",VERTEX,"E27.1.0.0");
            var Q29;
            Q29=sQuery(id+"F12.wireOp",VERTEX,"E27.1.0.1");
            var Q30;
            Q30=sQuery(id+"F12.wireOp",VERTEX,"E30.1.3.0");
            var Q31;
            Q31=sQuery(id+"F12.wireOp",VERTEX,"E27.3.0.2");
            var Q32;
            Q32=sQuery(id+"F12.wireOp",VERTEX,"E30.2.3.0");
            var Q33;
            Q33=sQuery(id+"F12.wireOp",VERTEX,"E27.3.0.3");
            var Q34;
            Q34=sQuery(id+"F12.wireOp",VERTEX,"E27.3.0.1");
            var Q35;
            Q35=sQuery(id+"F12.wireOp",VERTEX,"E30.3.3.0");
            var Q36;
            Q36=sQuery(id+"F12.wireOp",VERTEX,"E27.3.0.4");
            var Q37;
            Q37=sQuery(id+"F12.wireOp",VERTEX,"E27.3.0.5");
            var Q38;
            Q38=sQuery(id+"F12.wireOp",VERTEX,"E27.3.0.6");
            var Q39;
            Q39=sQuery(id+"F12.wireOp",VERTEX,"E27.4.0.2");
            var Q40;
            Q40=sQuery(id+"F12.wireOp",VERTEX,"E27.4.0.3");
            var Q41;
            Q41=sQuery(id+"F12.wireOp",VERTEX,"E27.4.0.5");
            var Q42;
            Q42=sQuery(id+"F12.wireOp",VERTEX,"E27.4.0.4");
            var Q43;
            Q43=sQuery(id+"F12.wireOp",VERTEX,"E30.3.4.0");
            var Q44;
            Q44=sQuery(id+"F12.wireOp",VERTEX,"E27.4.0.6");
            var Q45;
            Q45=sQuery(id+"F12.wireOp",VERTEX,"E30.1.4.0");
            var Q46;
            Q46=sQuery(id+"F12.wireOp",VERTEX,"E30.2.4.0");
            var Q47;
            Q47=sQuery(id+"F12.wireOp",VERTEX,"E27.5.0.5");
            var Q48;
            Q48=sQuery(id+"F12.wireOp",VERTEX,"E27.5.0.3");
            var Q49;
            Q49=sQuery(id+"F12.wireOp",VERTEX,"E27.5.0.4");
            var Q50;
            Q50=sQuery(id+"F12.wireOp",VERTEX,"E30.1.5.0");
            var Q51;
            Q51=sQuery(id+"F12.wireOp",VERTEX,"E30.3.5.0");
            var Q52;
            Q52=sQuery(id+"F12.wireOp",VERTEX,"E30.2.5.0");
            var Q53;
            Q53=sQuery(id+"F12.wireOp",VERTEX,"E27.5.0.6");
            var Q54;
            Q54=sQuery(id+"F12.wireOp",VERTEX,"E30.1.6.0");
            var Q55;
            Q55=sQuery(id+"F12.wireOp",VERTEX,"E30.3.6.0");
            var Q56;
            Q56=sQuery(id+"F12.wireOp",VERTEX,"E30.2.6.0");
            var Q57;
            Q57=sQuery(id+"F12.wireOp",VERTEX,"E27.6.0.4");
            var Q58;
            Q58=sQuery(id+"F12.wireOp",VERTEX,"E27.6.0.5");
            var Q59;
            Q59=sQuery(id+"F12.wireOp",VERTEX,"E27.6.0.6");
            var Q60;
            Q60=sQuery(id+"F12.wireOp",VERTEX,"E27.7.0.5");
            var Q61;
            Q61=sQuery(id+"F12.wireOp",VERTEX,"E27.7.0.6");
            var Q62;
            Q62=sQuery(id+"F12.wireOp",VERTEX,"E30.2.7.0");
            var Q63;
            Q63=sQuery(id+"F12.wireOp",VERTEX,"E30.3.7.0");
            var Q64;
            Q64=sQuery(id+"F12.wireOp",VERTEX,"E30.1.7.0");
            var Q65;
            Q65=sQuery(id+"F12.wireOp",VERTEX,"E27.8.0.6");
            var Q66;
            Q66=sQuery(id+"F12.wireOp",VERTEX,"E30.3.8.0");
            var Q67;
            Q67=sQuery(id+"F12.wireOp",VERTEX,"E30.1.8.0");
            var Q68;
            Q68=sQuery(id+"F12.wireOp",VERTEX,"E30.2.8.0");
            var Q69;
            Q69=sQuery(id+"F12.wireOp",VERTEX,"E30.1.9.0");
            var Q70;
            Q70=sQuery(id+"F12.wireOp",VERTEX,"E30.3.9.0");
            var Q71;
            Q71=sQuery(id+"F12.wireOp",VERTEX,"E30.2.9.0");
            var Q72;
            Q72=sQuery(id+"F12.wireOp",VERTEX,"E30.2.11.0");
            var Q73;
            Q73=sQuery(id+"F12.wireOp",VERTEX,"E30.1.13.0");
            var Q74;
            Q74=sQuery(id+"F12.wireOp",VERTEX,"E30.1.11.0");
            var Q75;
            Q75=sQuery(id+"F12.wireOp",VERTEX,"E30.2.13.0");
            var Q76;
            Q76=sQuery(id+"F12.wireOp",VERTEX,"E30.2.10.0");
            var Q77;
            Q77=sQuery(id+"F12.wireOp",VERTEX,"E30.1.10.0");
            var Q78;
            Q78=sQuery(id+"F12.wireOp",VERTEX,"E30.1.12.0");
            var Q79;
            Q79=sQuery(id+"F12.wireOp",VERTEX,"E30.2.12.0");
            var Q80;
            Q80=sQuery(id+"F12.wireOp",VERTEX,"E30.1.15.0");
            var Q81;
            Q81=sQuery(id+"F12.wireOp",VERTEX,"E30.1.17.0");
            var Q82;
            Q82=sQuery(id+"F12.wireOp",VERTEX,"E30.1.18.0");
            var Q83;
            Q83=sQuery(id+"F12.wireOp",VERTEX,"E30.1.16.0");
            var Q84;
            Q84=sQuery(id+"F12.wireOp",VERTEX,"E30.1.14.0");
            var Q85;
            Q85=makeQuery(id+"F6.opExtrude","SWEPT_BODY",BODY,{"disambiguationData":[OSD([sQuery(id+"F0.wireOp",EDGE,"E23.5.0.1"),sQuery(id+"F0.wireOp",EDGE,"E23.5.0.2"),sQuery(id+"F0.wireOp",EDGE,"E23.5.0.3"),sQuery(id+"F0.wireOp",EDGE,"E23.5.0.4"),sQuery(id+"F0.wireOp",EDGE,"E23.5.0.11"),sQuery(id+"F0.wireOp",EDGE,"E23.5.0.12"),sQuery(id+"F0.wireOp",EDGE,"E23.5.0.13"),sQuery(id+"F0.wireOp",EDGE,"E23.5.0.14"),sQuery(id+"F0.wireOp",EDGE,"E23.5.0.15"),sQuery(id+"F0.wireOp",EDGE,"E23.5.0.16"),sQuery(id+"F0.wireOp",EDGE,"E23.5.0.18"),sQuery(id+"F0.wireOp",EDGE,"E23.5.0.19"),sQuery(id+"F0.wireOp",EDGE,"E23.5.0.20"),sQuery(id+"F0.wireOp",EDGE,"E23.5.0.21"),sQuery(id+"F0.wireOp",EDGE,"E23.5.0.22"),sQuery(id+"F0.wireOp",EDGE,"E23.5.0.23"),sQuery(id+"F0.wireOp",EDGE,"E23.5.0.24"),sQuery(id+"F0.wireOp",EDGE,"E23.5.0.25"),sQuery(id+"F0.wireOp",EDGE,"E23.5.0.26"),sQuery(id+"F0.wireOp",EDGE,"E23.5.0.27")])]});
            var Q86;
            Q86=makeQuery(id+"F10.opExtrude","SWEPT_BODY",BODY,{"disambiguationData":[OSD([sQuery(id+"F0.wireOp",EDGE,"E24.3.9.0"),sQuery(id+"F0.wireOp",EDGE,"E24.6.9.0"),sQuery(id+"F0.wireOp",EDGE,"E24.9.9.0"),sQuery(id+"F0.wireOp",EDGE,"E24.12.9.0"),sQuery(id+"F0.wireOp",EDGE,"E24.21.9.0"),sQuery(id+"F0.wireOp",EDGE,"E24.24.9.0"),sQuery(id+"F0.wireOp",EDGE,"E24.27.9.0"),sQuery(id+"F0.wireOp",EDGE,"E24.30.9.0"),sQuery(id+"F0.wireOp",EDGE,"E24.33.9.0"),sQuery(id+"F0.wireOp",EDGE,"E24.36.9.0"),sQuery(id+"F0.wireOp",EDGE,"E24.43.9.0"),sQuery(id+"F0.wireOp",EDGE,"E24.46.9.0"),sQuery(id+"F0.wireOp",EDGE,"E24.49.9.0"),sQuery(id+"F0.wireOp",EDGE,"E24.52.9.0"),sQuery(id+"F0.wireOp",EDGE,"E24.56.9.0"),sQuery(id+"F0.wireOp",EDGE,"E24.59.9.0"),sQuery(id+"F0.wireOp",EDGE,"E24.63.9.0"),sQuery(id+"F0.wireOp",EDGE,"E24.66.9.0"),sQuery(id+"F0.wireOp",EDGE,"E24.70.9.0"),sQuery(id+"F0.wireOp",EDGE,"E24.74.9.0")])]});
            var Q87;
            Q87=makeQuery(id+"F2.opExtrude","SWEPT_BODY",BODY,{"disambiguationData":[OSD([sQuery(id+"F0.wireOp",EDGE,"E23.1.0.1"),sQuery(id+"F0.wireOp",EDGE,"E23.1.0.2"),sQuery(id+"F0.wireOp",EDGE,"E23.1.0.3"),sQuery(id+"F0.wireOp",EDGE,"E23.1.0.4"),sQuery(id+"F0.wireOp",EDGE,"E23.1.0.11"),sQuery(id+"F0.wireOp",EDGE,"E23.1.0.12"),sQuery(id+"F0.wireOp",EDGE,"E23.1.0.13"),sQuery(id+"F0.wireOp",EDGE,"E23.1.0.14"),sQuery(id+"F0.wireOp",EDGE,"E23.1.0.15"),sQuery(id+"F0.wireOp",EDGE,"E23.1.0.16"),sQuery(id+"F0.wireOp",EDGE,"E23.1.0.18"),sQuery(id+"F0.wireOp",EDGE,"E23.1.0.19"),sQuery(id+"F0.wireOp",EDGE,"E23.1.0.20"),sQuery(id+"F0.wireOp",EDGE,"E23.1.0.21"),sQuery(id+"F0.wireOp",EDGE,"E23.1.0.22"),sQuery(id+"F0.wireOp",EDGE,"E23.1.0.23"),sQuery(id+"F0.wireOp",EDGE,"E23.1.0.24"),sQuery(id+"F0.wireOp",EDGE,"E23.1.0.25"),sQuery(id+"F0.wireOp",EDGE,"E23.1.0.26"),sQuery(id+"F0.wireOp",EDGE,"E23.1.0.27")])]});
            var Q88;
            Q88=makeQuery(id+"F5.opExtrude","SWEPT_BODY",BODY,{"disambiguationData":[OSD([sQuery(id+"F0.wireOp",EDGE,"E23.4.0.1"),sQuery(id+"F0.wireOp",EDGE,"E23.4.0.2"),sQuery(id+"F0.wireOp",EDGE,"E23.4.0.3"),sQuery(id+"F0.wireOp",EDGE,"E23.4.0.4"),sQuery(id+"F0.wireOp",EDGE,"E23.4.0.11"),sQuery(id+"F0.wireOp",EDGE,"E23.4.0.12"),sQuery(id+"F0.wireOp",EDGE,"E23.4.0.13"),sQuery(id+"F0.wireOp",EDGE,"E23.4.0.14"),sQuery(id+"F0.wireOp",EDGE,"E23.4.0.15"),sQuery(id+"F0.wireOp",EDGE,"E23.4.0.16"),sQuery(id+"F0.wireOp",EDGE,"E23.4.0.18"),sQuery(id+"F0.wireOp",EDGE,"E23.4.0.19"),sQuery(id+"F0.wireOp",EDGE,"E23.4.0.20"),sQuery(id+"F0.wireOp",EDGE,"E23.4.0.21"),sQuery(id+"F0.wireOp",EDGE,"E23.4.0.22"),sQuery(id+"F0.wireOp",EDGE,"E23.4.0.23"),sQuery(id+"F0.wireOp",EDGE,"E23.4.0.24"),sQuery(id+"F0.wireOp",EDGE,"E23.4.0.25"),sQuery(id+"F0.wireOp",EDGE,"E23.4.0.26"),sQuery(id+"F0.wireOp",EDGE,"E23.4.0.27")])]});
            var Q89;
            Q89=makeQuery(id+"F11.opExtrude","SWEPT_BODY",BODY,{"disambiguationData":[OSD([sQuery(id+"F0.wireOp",EDGE,"E24.3.10.0"),sQuery(id+"F0.wireOp",EDGE,"E24.6.10.0"),sQuery(id+"F0.wireOp",EDGE,"E24.9.10.0"),sQuery(id+"F0.wireOp",EDGE,"E24.12.10.0"),sQuery(id+"F0.wireOp",EDGE,"E24.21.10.0"),sQuery(id+"F0.wireOp",EDGE,"E24.24.10.0"),sQuery(id+"F0.wireOp",EDGE,"E24.27.10.0"),sQuery(id+"F0.wireOp",EDGE,"E24.30.10.0"),sQuery(id+"F0.wireOp",EDGE,"E24.33.10.0"),sQuery(id+"F0.wireOp",EDGE,"E24.36.10.0"),sQuery(id+"F0.wireOp",EDGE,"E24.43.10.0"),sQuery(id+"F0.wireOp",EDGE,"E24.46.10.0"),sQuery(id+"F0.wireOp",EDGE,"E24.49.10.0"),sQuery(id+"F0.wireOp",EDGE,"E24.52.10.0"),sQuery(id+"F0.wireOp",EDGE,"E24.56.10.0"),sQuery(id+"F0.wireOp",EDGE,"E24.59.10.0"),sQuery(id+"F0.wireOp",EDGE,"E24.63.10.0"),sQuery(id+"F0.wireOp",EDGE,"E24.66.10.0"),sQuery(id+"F0.wireOp",EDGE,"E24.70.10.0"),sQuery(id+"F0.wireOp",EDGE,"E24.74.10.0")])]});
            var Q90;
            Q90=makeQuery(id+"F7.opExtrude","SWEPT_BODY",BODY,{"disambiguationData":[OSD([sQuery(id+"F0.wireOp",EDGE,"E23.6.0.1"),sQuery(id+"F0.wireOp",EDGE,"E23.6.0.2"),sQuery(id+"F0.wireOp",EDGE,"E23.6.0.3"),sQuery(id+"F0.wireOp",EDGE,"E23.6.0.4"),sQuery(id+"F0.wireOp",EDGE,"E23.6.0.11"),sQuery(id+"F0.wireOp",EDGE,"E23.6.0.12"),sQuery(id+"F0.wireOp",EDGE,"E23.6.0.13"),sQuery(id+"F0.wireOp",EDGE,"E23.6.0.14"),sQuery(id+"F0.wireOp",EDGE,"E23.6.0.15"),sQuery(id+"F0.wireOp",EDGE,"E23.6.0.16"),sQuery(id+"F0.wireOp",EDGE,"E23.6.0.18"),sQuery(id+"F0.wireOp",EDGE,"E23.6.0.19"),sQuery(id+"F0.wireOp",EDGE,"E23.6.0.20"),sQuery(id+"F0.wireOp",EDGE,"E23.6.0.21"),sQuery(id+"F0.wireOp",EDGE,"E23.6.0.22"),sQuery(id+"F0.wireOp",EDGE,"E23.6.0.23"),sQuery(id+"F0.wireOp",EDGE,"E23.6.0.24"),sQuery(id+"F0.wireOp",EDGE,"E23.6.0.25"),sQuery(id+"F0.wireOp",EDGE,"E23.6.0.26"),sQuery(id+"F0.wireOp",EDGE,"E23.6.0.27")])]});
            var Q91;
            Q91=makeQuery(id+"F9.opExtrude","SWEPT_BODY",BODY,{"disambiguationData":[OSD([sQuery(id+"F0.wireOp",EDGE,"E24.3.8.0"),sQuery(id+"F0.wireOp",EDGE,"E24.6.8.0"),sQuery(id+"F0.wireOp",EDGE,"E24.9.8.0"),sQuery(id+"F0.wireOp",EDGE,"E24.12.8.0"),sQuery(id+"F0.wireOp",EDGE,"E24.21.8.0"),sQuery(id+"F0.wireOp",EDGE,"E24.24.8.0"),sQuery(id+"F0.wireOp",EDGE,"E24.27.8.0"),sQuery(id+"F0.wireOp",EDGE,"E24.30.8.0"),sQuery(id+"F0.wireOp",EDGE,"E24.33.8.0"),sQuery(id+"F0.wireOp",EDGE,"E24.36.8.0"),sQuery(id+"F0.wireOp",EDGE,"E24.43.8.0"),sQuery(id+"F0.wireOp",EDGE,"E24.46.8.0"),sQuery(id+"F0.wireOp",EDGE,"E24.49.8.0"),sQuery(id+"F0.wireOp",EDGE,"E24.52.8.0"),sQuery(id+"F0.wireOp",EDGE,"E24.56.8.0"),sQuery(id+"F0.wireOp",EDGE,"E24.59.8.0"),sQuery(id+"F0.wireOp",EDGE,"E24.63.8.0"),sQuery(id+"F0.wireOp",EDGE,"E24.66.8.0"),sQuery(id+"F0.wireOp",EDGE,"E24.70.8.0"),sQuery(id+"F0.wireOp",EDGE,"E24.74.8.0")])]});
            var Q92;
            Q92=makeQuery(id+"F3.opExtrude","SWEPT_BODY",BODY,{"disambiguationData":[OSD([sQuery(id+"F0.wireOp",EDGE,"E23.2.0.1"),sQuery(id+"F0.wireOp",EDGE,"E23.2.0.2"),sQuery(id+"F0.wireOp",EDGE,"E23.2.0.3"),sQuery(id+"F0.wireOp",EDGE,"E23.2.0.4"),sQuery(id+"F0.wireOp",EDGE,"E23.2.0.11"),sQuery(id+"F0.wireOp",EDGE,"E23.2.0.12"),sQuery(id+"F0.wireOp",EDGE,"E23.2.0.13"),sQuery(id+"F0.wireOp",EDGE,"E23.2.0.14"),sQuery(id+"F0.wireOp",EDGE,"E23.2.0.15"),sQuery(id+"F0.wireOp",EDGE,"E23.2.0.16"),sQuery(id+"F0.wireOp",EDGE,"E23.2.0.18"),sQuery(id+"F0.wireOp",EDGE,"E23.2.0.19"),sQuery(id+"F0.wireOp",EDGE,"E23.2.0.20"),sQuery(id+"F0.wireOp",EDGE,"E23.2.0.21"),sQuery(id+"F0.wireOp",EDGE,"E23.2.0.22"),sQuery(id+"F0.wireOp",EDGE,"E23.2.0.23"),sQuery(id+"F0.wireOp",EDGE,"E23.2.0.24"),sQuery(id+"F0.wireOp",EDGE,"E23.2.0.25"),sQuery(id+"F0.wireOp",EDGE,"E23.2.0.26"),sQuery(id+"F0.wireOp",EDGE,"E23.2.0.27")])]});
            var Q93;
            Q93=makeQuery(id+"F8.opExtrude","SWEPT_BODY",BODY,{"disambiguationData":[OSD([sQuery(id+"F0.wireOp",EDGE,"E24.3.7.0"),sQuery(id+"F0.wireOp",EDGE,"E24.6.7.0"),sQuery(id+"F0.wireOp",EDGE,"E24.9.7.0"),sQuery(id+"F0.wireOp",EDGE,"E24.12.7.0"),sQuery(id+"F0.wireOp",EDGE,"E24.21.7.0"),sQuery(id+"F0.wireOp",EDGE,"E24.24.7.0"),sQuery(id+"F0.wireOp",EDGE,"E24.27.7.0"),sQuery(id+"F0.wireOp",EDGE,"E24.30.7.0"),sQuery(id+"F0.wireOp",EDGE,"E24.33.7.0"),sQuery(id+"F0.wireOp",EDGE,"E24.36.7.0"),sQuery(id+"F0.wireOp",EDGE,"E24.43.7.0"),sQuery(id+"F0.wireOp",EDGE,"E24.46.7.0"),sQuery(id+"F0.wireOp",EDGE,"E24.49.7.0"),sQuery(id+"F0.wireOp",EDGE,"E24.52.7.0"),sQuery(id+"F0.wireOp",EDGE,"E24.56.7.0"),sQuery(id+"F0.wireOp",EDGE,"E24.59.7.0"),sQuery(id+"F0.wireOp",EDGE,"E24.63.7.0"),sQuery(id+"F0.wireOp",EDGE,"E24.66.7.0"),sQuery(id+"F0.wireOp",EDGE,"E24.70.7.0"),sQuery(id+"F0.wireOp",EDGE,"E24.74.7.0")])]});
            var Q94;
            Q94=makeQuery(id+"F1.opExtrude","SWEPT_BODY",BODY,{"disambiguationData":[OSD([sQuery(id+"F0.wireOp",EDGE,"E1.bottom"),sQuery(id+"F0.wireOp",EDGE,"E1.top"),sQuery(id+"F0.wireOp",EDGE,"E1.left"),sQuery(id+"F0.wireOp",EDGE,"E1.right"),sQuery(id+"F0.wireOp",EDGE,"E2"),sQuery(id+"F0.wireOp",EDGE,"E3"),sQuery(id+"F0.wireOp",EDGE,"E4"),sQuery(id+"F0.wireOp",EDGE,"E5"),sQuery(id+"F0.wireOp",EDGE,"E6"),sQuery(id+"F0.wireOp",EDGE,"E7"),sQuery(id+"F0.wireOp",EDGE,"E8"),sQuery(id+"F0.wireOp",EDGE,"E9.MirrorCS"),sQuery(id+"F0.wireOp",EDGE,"E10.MirrorCS"),sQuery(id+"F0.wireOp",EDGE,"E11.MirrorCS"),sQuery(id+"F0.wireOp",EDGE,"E13.trimOffspring"),sQuery(id+"F0.wireOp",EDGE,"E14.trimOffspring"),sQuery(id+"F0.wireOp",EDGE,"E16.trimOffspring"),sQuery(id+"F0.wireOp",EDGE,"E17.trimOffspring"),sQuery(id+"F0.wireOp",EDGE,"E20"),sQuery(id+"F0.wireOp",EDGE,"E21")])]});
            var Q95;
            Q95=makeQuery(id+"F4.opExtrude","SWEPT_BODY",BODY,{"disambiguationData":[OSD([sQuery(id+"F0.wireOp",EDGE,"E23.3.0.1"),sQuery(id+"F0.wireOp",EDGE,"E23.3.0.2"),sQuery(id+"F0.wireOp",EDGE,"E23.3.0.3"),sQuery(id+"F0.wireOp",EDGE,"E23.3.0.4"),sQuery(id+"F0.wireOp",EDGE,"E23.3.0.11"),sQuery(id+"F0.wireOp",EDGE,"E23.3.0.12"),sQuery(id+"F0.wireOp",EDGE,"E23.3.0.13"),sQuery(id+"F0.wireOp",EDGE,"E23.3.0.14"),sQuery(id+"F0.wireOp",EDGE,"E23.3.0.15"),sQuery(id+"F0.wireOp",EDGE,"E23.3.0.16"),sQuery(id+"F0.wireOp",EDGE,"E23.3.0.18"),sQuery(id+"F0.wireOp",EDGE,"E23.3.0.19"),sQuery(id+"F0.wireOp",EDGE,"E23.3.0.20"),sQuery(id+"F0.wireOp",EDGE,"E23.3.0.21"),sQuery(id+"F0.wireOp",EDGE,"E23.3.0.22"),sQuery(id+"F0.wireOp",EDGE,"E23.3.0.23"),sQuery(id+"F0.wireOp",EDGE,"E23.3.0.24"),sQuery(id+"F0.wireOp",EDGE,"E23.3.0.25"),sQuery(id+"F0.wireOp",EDGE,"E23.3.0.26"),sQuery(id+"F0.wireOp",EDGE,"E23.3.0.27")])]});
            hole(context, id + "F13", {"style" : HoleStyle.C_BORE, "endStyle" : HoleEndStyle.THROUGH, "holeDiameter" : 3.5 * mm, "cBoreDiameter" : 6 * mm, "cBoreDepth" : 3.5 * mm, "majorDiameter" : 5 * mm, "isTappedThrough" : true, "tappedDepth" : 12 * mm, "tapClearance" : 3, "locations" : qUnion([Q0, Q1, Q2, Q3, Q4, Q5, Q6, Q7, Q8, Q9, Q10, Q11, Q12, Q13, Q14, Q15, Q16, Q17, Q18, Q19, Q20, Q21, Q22, Q23, Q24, Q25, Q26, Q27, Q28, Q29, Q30, Q31, Q32, Q33, Q34, Q35, Q36, Q37, Q38, Q39, Q40, Q41, Q42, Q43, Q44, Q45, Q46, Q47, Q48, Q49, Q50, Q51, Q52, Q53, Q54, Q55, Q56, Q57, Q58, Q59, Q60, Q61, Q62, Q63, Q64, Q65, Q66, Q67, Q68, Q69, Q70, Q71, Q72, Q73, Q74, Q75, Q76, Q77, Q78, Q79, Q80, Q81, Q82, Q83, Q84]), "scope" : qUnion([Q85, Q86, Q87, Q88, Q89, Q90, Q91, Q92, Q93, Q94, Q95])});
        }
        {
            var Q0;
            Q0=sQuery(id+"F12.wireOp",VERTEX,"E28.0.10.0");
            var Q1;
            Q1=sQuery(id+"F12.wireOp",VERTEX,"E30.0.24.0");
            var Q2;
            Q2=sQuery(id+"F12.wireOp",VERTEX,"E30.0.12.0");
            var Q3;
            Q3=sQuery(id+"F12.wireOp",VERTEX,"E30.0.16.0");
            var Q4;
            Q4=sQuery(id+"F12.wireOp",VERTEX,"E30.0.33.0");
            var Q5;
            Q5=sQuery(id+"F12.wireOp",VERTEX,"E30.0.32.0");
            var Q6;
            Q6=sQuery(id+"F12.wireOp",VERTEX,"E30.0.36.0");
            var Q7;
            Q7=sQuery(id+"F12.wireOp",VERTEX,"E30.0.28.0");
            var Q8;
            Q8=sQuery(id+"F12.wireOp",VERTEX,"E30.0.37.0");
            var Q9;
            Q9=sQuery(id+"F12.wireOp",VERTEX,"E30.0.4.0");
            var Q10;
            Q10=sQuery(id+"F12.wireOp",VERTEX,"E30.0.8.0");
            var Q11;
            Q11=sQuery(id+"F12.wireOp",VERTEX,"E30.0.20.0");
            var Q12;
            Q12=sQuery(id+"F12.wireOp",VERTEX,"E30.0.5.0");
            var Q13;
            Q13=sQuery(id+"F12.wireOp",VERTEX,"E29.1.0.0");
            var Q14;
            Q14=sQuery(id+"F12.wireOp",VERTEX,"E30.0.21.0");
            var Q15;
            Q15=sQuery(id+"F12.wireOp",VERTEX,"E30.0.17.0");
            var Q16;
            Q16=sQuery(id+"F12.wireOp",VERTEX,"E30.0.13.0");
            var Q17;
            Q17=sQuery(id+"F12.wireOp",VERTEX,"E30.0.9.0");
            var Q18;
            Q18=sQuery(id+"F12.wireOp",VERTEX,"E30.0.29.0");
            var Q19;
            Q19=sQuery(id+"F12.wireOp",VERTEX,"E30.0.25.0");
            var Q20;
            Q20=sQuery(id+"F12.wireOp",VERTEX,"E30.0.6.0");
            var Q21;
            Q21=sQuery(id+"F12.wireOp",VERTEX,"E29.2.0.0");
            var Q22;
            Q22=sQuery(id+"F12.wireOp",VERTEX,"E30.0.22.0");
            var Q23;
            Q23=sQuery(id+"F12.wireOp",VERTEX,"E30.0.18.0");
            var Q24;
            Q24=sQuery(id+"F12.wireOp",VERTEX,"E30.0.14.0");
            var Q25;
            Q25=sQuery(id+"F12.wireOp",VERTEX,"E30.0.10.0");
            var Q26;
            Q26=sQuery(id+"F12.wireOp",VERTEX,"E30.0.30.0");
            var Q27;
            Q27=sQuery(id+"F12.wireOp",VERTEX,"E30.0.26.0");
            var Q28;
            Q28=sQuery(id+"F12.wireOp",VERTEX,"E30.0.38.0");
            var Q29;
            Q29=sQuery(id+"F12.wireOp",VERTEX,"E30.0.34.0");
            var Q30;
            Q30=sQuery(id+"F12.wireOp",VERTEX,"E30.0.15.0");
            var Q31;
            Q31=sQuery(id+"F12.wireOp",VERTEX,"E30.0.11.0");
            var Q32;
            Q32=sQuery(id+"F12.wireOp",VERTEX,"E30.0.7.0");
            var Q33;
            Q33=sQuery(id+"F12.wireOp",VERTEX,"E30.0.3.0");
            var Q34;
            Q34=sQuery(id+"F12.wireOp",VERTEX,"E30.0.31.0");
            var Q35;
            Q35=sQuery(id+"F12.wireOp",VERTEX,"E30.0.27.0");
            var Q36;
            Q36=sQuery(id+"F12.wireOp",VERTEX,"E30.0.23.0");
            var Q37;
            Q37=sQuery(id+"F12.wireOp",VERTEX,"E30.0.19.0");
            var Q38;
            Q38=sQuery(id+"F12.wireOp",VERTEX,"E30.0.39.0");
            var Q39;
            Q39=sQuery(id+"F12.wireOp",VERTEX,"E30.0.35.0");
            var Q40;
            Q40=sQuery(id+"F12.wireOp",VERTEX,"E31.0.42.0");
            var Q41;
            Q41=sQuery(id+"F12.wireOp",VERTEX,"E31.0.43.0");
            var Q42;
            Q42=sQuery(id+"F12.wireOp",VERTEX,"E31.0.48.0");
            var Q43;
            Q43=sQuery(id+"F12.wireOp",VERTEX,"E31.0.44.0");
            var Q44;
            Q44=sQuery(id+"F12.wireOp",VERTEX,"E31.0.41.0");
            var Q45;
            Q45=sQuery(id+"F12.wireOp",VERTEX,"E31.0.49.0");
            var Q46;
            Q46=sQuery(id+"F12.wireOp",VERTEX,"E31.0.45.0");
            var Q47;
            Q47=sQuery(id+"F12.wireOp",VERTEX,"E31.0.46.0");
            var Q48;
            Q48=sQuery(id+"F12.wireOp",VERTEX,"E31.0.47.0");
            var Q49;
            Q49=sQuery(id+"F12.wireOp",VERTEX,"E31.0.40.0");
            var Q50;
            Q50=makeQuery(id+"F11.opExtrude","SWEPT_BODY",BODY,{"disambiguationData":[OSD([sQuery(id+"F0.wireOp",EDGE,"E24.3.10.0"),sQuery(id+"F0.wireOp",EDGE,"E24.6.10.0"),sQuery(id+"F0.wireOp",EDGE,"E24.9.10.0"),sQuery(id+"F0.wireOp",EDGE,"E24.12.10.0"),sQuery(id+"F0.wireOp",EDGE,"E24.21.10.0"),sQuery(id+"F0.wireOp",EDGE,"E24.24.10.0"),sQuery(id+"F0.wireOp",EDGE,"E24.27.10.0"),sQuery(id+"F0.wireOp",EDGE,"E24.30.10.0"),sQuery(id+"F0.wireOp",EDGE,"E24.33.10.0"),sQuery(id+"F0.wireOp",EDGE,"E24.36.10.0"),sQuery(id+"F0.wireOp",EDGE,"E24.43.10.0"),sQuery(id+"F0.wireOp",EDGE,"E24.46.10.0"),sQuery(id+"F0.wireOp",EDGE,"E24.49.10.0"),sQuery(id+"F0.wireOp",EDGE,"E24.52.10.0"),sQuery(id+"F0.wireOp",EDGE,"E24.56.10.0"),sQuery(id+"F0.wireOp",EDGE,"E24.59.10.0"),sQuery(id+"F0.wireOp",EDGE,"E24.63.10.0"),sQuery(id+"F0.wireOp",EDGE,"E24.66.10.0"),sQuery(id+"F0.wireOp",EDGE,"E24.70.10.0"),sQuery(id+"F0.wireOp",EDGE,"E24.74.10.0")])]});
            hole(context, id + "F14", {"style" : HoleStyle.C_BORE, "endStyle" : HoleEndStyle.THROUGH, "holeDiameter" : 3.5 * mm, "cBoreDiameter" : 6 * mm, "cBoreDepth" : 3.5 * mm, "majorDiameter" : 5 * mm, "isTappedThrough" : true, "tappedDepth" : 12 * mm, "tapClearance" : 3, "locations" : qUnion([Q0, Q1, Q2, Q3, Q4, Q5, Q6, Q7, Q8, Q9, Q10, Q11, Q12, Q13, Q14, Q15, Q16, Q17, Q18, Q19, Q20, Q21, Q22, Q23, Q24, Q25, Q26, Q27, Q28, Q29, Q30, Q31, Q32, Q33, Q34, Q35, Q36, Q37, Q38, Q39, Q40, Q41, Q42, Q43, Q44, Q45, Q46, Q47, Q48, Q49]), "scope" : qUnion([Q50])});
        }
    });
